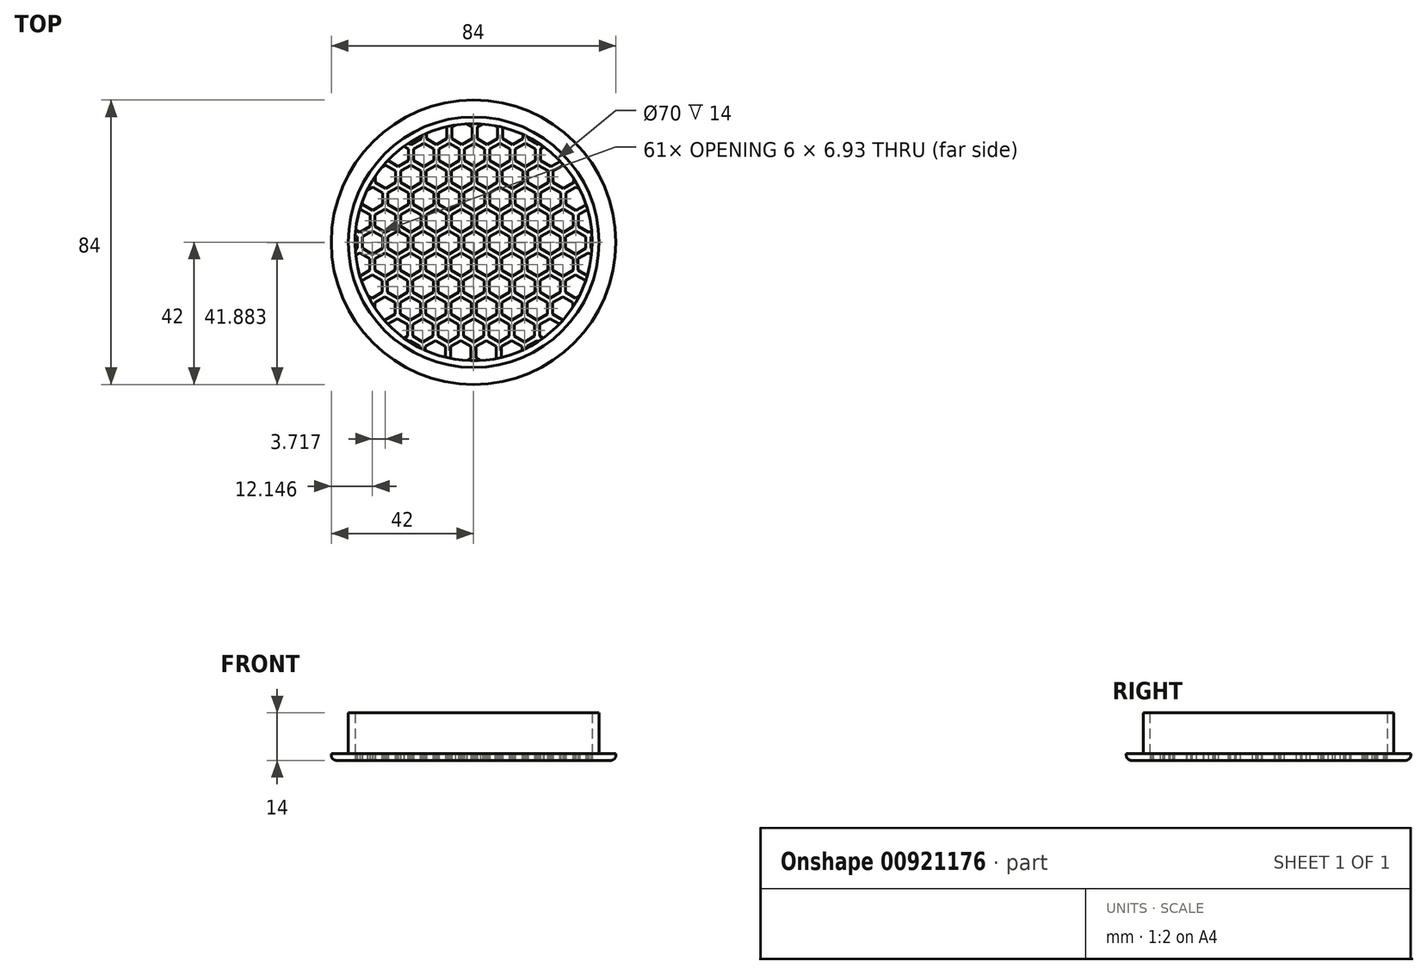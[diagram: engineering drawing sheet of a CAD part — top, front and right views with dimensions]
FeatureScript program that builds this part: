
annotation { "Feature Type Name" : "Feature", "Feature Type Description" : "" }
export const myFeature = defineFeature(function(context is Context, id is Id, definition is map)
    precondition{}
    {
        {
            var Q0;
            Q0=qCreatedBy(makeId("Top.planeOp"),FACE);
            var sketch = newSketch(context, id + "F0", { "sketchPlane" : qUnion([Q0])});
            skCircle(sketch, "E0", {"center": v(0, 0) * mm, "radius": 42 * mm});
            skCircle(sketch, "E1", {"center": v(0, 0) * mm, "radius": 35 * mm});
            skSolve(sketch);
        }
        {
            var Q0;
            Q0=makeQuery(id+"F0.imprint","IMPRINT",FACE,{"disambiguationData":[TD([[makeQuery(id+"F0.imprint","IMPRINT",EDGE,{"derivedFrom":sQuery(id+"F0.wireOp",EDGE,"E0")}),1.0]])]});
            extrude(context, id + "F1", {"entities" : qUnion([Q0]), "depth" : 2 * mm, "offsetDistance" : 25 * mm});
        }
        {
            var Q0;
            Q0=makeQuery(id+"F1.opExtrude","CAP_EDGE",EDGE,{"disambiguationData":[OSD([sQuery(id+"F0.wireOp",EDGE,"E0")])],"isStart":true});
            fillet(context, id + "F2", {"entities" : qUnion([Q0]), "radius" : 1.5 * mm, "tangentPropagation" : true, "allowEdgeOverflow" : false});
        }
        {
            var Q0;
            Q0=makeQuery(id+"F1.opExtrude","CAP_FACE",FACE,{"disambiguationData":[OSD([sQuery(id+"F0.wireOp",EDGE,"E0"),sQuery(id+"F0.wireOp",EDGE,"E1")])],"isStart":false});
            var sketch = newSketch(context, id + "F3", { "sketchPlane" : qUnion([Q0])});
            skCircle(sketch, "E2", {"center": v(0, 0) * mm, "radius": 37 * mm});
            skCircle(sketch, "E3", {"center": v(0, 0) * mm, "radius": 35 * mm});
            skSolve(sketch);
        }
        {
            var Q0;
            Q0=makeQuery(id+"F3.imprint","IMPRINT",FACE,{"disambiguationData":[TD([[makeQuery(id+"F3.imprint","IMPRINT",EDGE,{"derivedFrom":sQuery(id+"F3.wireOp",EDGE,"E2")}),1.0]])]});
            extrude(context, id + "F4", {"entities" : qUnion([Q0]), "operationType" : NewBodyOperationType.ADD, "depth" : 12 * mm, "offsetDistance" : 25 * mm});
        }
        {
            var Q0;
            Q0=qCreatedBy(makeId("Top.planeOp"),FACE);
            var sketch = newSketch(context, id + "F5", { "sketchPlane" : qUnion([Q0])});
            skLineSegment(sketch, "E4.4.0.0", {"start": v(-56.27, -29.03) * mm, "end": v(-53.27, -30.77) * mm});
            skPoint(sketch, "E4.4.0.1", {"position": v(-54.77, -35.1) * mm});
            skCircle(sketch, "E4.4.0.2", {"center": v(-56.27, -32.5) * mm, "radius": 3 * mm, "construction": true});
            skLineSegment(sketch, "E4.4.0.3", {"start": v(-53.27, -30.77) * mm, "end": v(-53.27, -34.23) * mm});
            skLineSegment(sketch, "E4.4.0.4", {"start": v(-59.27, -34.23) * mm, "end": v(-59.27, -30.77) * mm});
            skLineSegment(sketch, "E4.4.0.5", {"start": v(-59.27, -30.77) * mm, "end": v(-56.27, -29.03) * mm});
            skLineSegment(sketch, "E4.4.0.6", {"start": v(-53.27, -34.23) * mm, "end": v(-56.27, -35.96) * mm});
            skLineSegment(sketch, "E4.4.0.7", {"start": v(-56.27, -35.96) * mm, "end": v(-59.27, -34.23) * mm});
            skLineSegment(sketch, "E5.0.1.0", {"start": v(-55.49, -27.75) * mm, "end": v(-55.49, -24.29) * mm});
            skCircle(sketch, "E5.0.1.1", {"center": v(-52.49, -26.02) * mm, "radius": 3 * mm, "construction": true});
            skPoint(sketch, "E5.0.1.2", {"position": v(-50.99, -28.62) * mm});
            skLineSegment(sketch, "E5.0.1.3", {"start": v(-52.49, -29.49) * mm, "end": v(-55.49, -27.75) * mm});
            skLineSegment(sketch, "E5.0.1.4", {"start": v(-52.49, -22.56) * mm, "end": v(-49.49, -24.29) * mm});
            skLineSegment(sketch, "E5.0.1.5", {"start": v(-55.49, -24.29) * mm, "end": v(-52.49, -22.56) * mm});
            skLineSegment(sketch, "E5.0.1.6", {"start": v(-49.49, -24.29) * mm, "end": v(-49.49, -27.75) * mm});
            skLineSegment(sketch, "E5.0.1.7", {"start": v(-49.49, -27.75) * mm, "end": v(-52.49, -29.49) * mm});
            skLineSegment(sketch, "E5.0.2.0", {"start": v(-51.7, -21.28) * mm, "end": v(-51.7, -17.81) * mm});
            skCircle(sketch, "E5.0.2.1", {"center": v(-48.7, -19.55) * mm, "radius": 3 * mm, "construction": true});
            skPoint(sketch, "E5.0.2.2", {"position": v(-47.2, -22.14) * mm});
            skLineSegment(sketch, "E5.0.2.3", {"start": v(-48.7, -23) * mm, "end": v(-51.7, -21.28) * mm});
            skLineSegment(sketch, "E5.0.2.4", {"start": v(-48.7, -16.08) * mm, "end": v(-45.7, -17.81) * mm});
            skLineSegment(sketch, "E5.0.2.5", {"start": v(-51.7, -17.81) * mm, "end": v(-48.7, -16.08) * mm});
            skLineSegment(sketch, "E5.0.2.6", {"start": v(-45.7, -17.81) * mm, "end": v(-45.7, -21.28) * mm});
            skLineSegment(sketch, "E5.0.2.7", {"start": v(-45.7, -21.28) * mm, "end": v(-48.7, -23) * mm});
            skLineSegment(sketch, "E5.0.3.0", {"start": v(-47.92, -14.8) * mm, "end": v(-47.92, -11.34) * mm});
            skCircle(sketch, "E5.0.3.1", {"center": v(-44.92, -13.07) * mm, "radius": 3 * mm, "construction": true});
            skPoint(sketch, "E5.0.3.2", {"position": v(-43.42, -15.67) * mm});
            skLineSegment(sketch, "E5.0.3.3", {"start": v(-44.92, -16.53) * mm, "end": v(-47.92, -14.8) * mm});
            skLineSegment(sketch, "E5.0.3.4", {"start": v(-44.92, -9.6) * mm, "end": v(-41.92, -11.34) * mm});
            skLineSegment(sketch, "E5.0.3.5", {"start": v(-47.92, -11.34) * mm, "end": v(-44.92, -9.6) * mm});
            skLineSegment(sketch, "E5.0.3.6", {"start": v(-41.92, -11.34) * mm, "end": v(-41.92, -14.8) * mm});
            skLineSegment(sketch, "E5.0.3.7", {"start": v(-41.92, -14.8) * mm, "end": v(-44.92, -16.53) * mm});
            skLineSegment(sketch, "E5.0.4.0", {"start": v(-44.14, -8.33) * mm, "end": v(-44.14, -4.86) * mm});
            skCircle(sketch, "E5.0.4.1", {"center": v(-41.14, -6.6) * mm, "radius": 3 * mm, "construction": true});
            skPoint(sketch, "E5.0.4.2", {"position": v(-39.64, -9.2) * mm});
            skLineSegment(sketch, "E5.0.4.3", {"start": v(-41.14, -10.06) * mm, "end": v(-44.14, -8.33) * mm});
            skLineSegment(sketch, "E5.0.4.4", {"start": v(-41.14, -3.13) * mm, "end": v(-38.14, -4.86) * mm});
            skLineSegment(sketch, "E5.0.4.5", {"start": v(-44.14, -4.86) * mm, "end": v(-41.14, -3.13) * mm});
            skLineSegment(sketch, "E5.0.4.6", {"start": v(-38.14, -4.86) * mm, "end": v(-38.14, -8.33) * mm});
            skLineSegment(sketch, "E5.0.4.7", {"start": v(-38.14, -8.33) * mm, "end": v(-41.14, -10.06) * mm});
            skLineSegment(sketch, "E5.0.5.0", {"start": v(-40.35, -1.85) * mm, "end": v(-40.35, 1.62) * mm});
            skCircle(sketch, "E5.0.5.1", {"center": v(-37.35, -0.12) * mm, "radius": 3 * mm, "construction": true});
            skPoint(sketch, "E5.0.5.2", {"position": v(-35.85, -2.72) * mm});
            skLineSegment(sketch, "E5.0.5.3", {"start": v(-37.35, -3.58) * mm, "end": v(-40.35, -1.85) * mm});
            skLineSegment(sketch, "E5.0.5.4", {"start": v(-37.35, 3.35) * mm, "end": v(-34.35, 1.62) * mm});
            skLineSegment(sketch, "E5.0.5.5", {"start": v(-40.35, 1.62) * mm, "end": v(-37.35, 3.35) * mm});
            skLineSegment(sketch, "E5.0.5.6", {"start": v(-34.35, 1.62) * mm, "end": v(-34.35, -1.85) * mm});
            skLineSegment(sketch, "E5.0.5.7", {"start": v(-34.35, -1.85) * mm, "end": v(-37.35, -3.58) * mm});
            skLineSegment(sketch, "E5.0.6.0", {"start": v(-36.57, 4.63) * mm, "end": v(-36.57, 8.1) * mm});
            skCircle(sketch, "E5.0.6.1", {"center": v(-33.57, 6.36) * mm, "radius": 3 * mm, "construction": true});
            skPoint(sketch, "E5.0.6.2", {"position": v(-32.07, 3.76) * mm});
            skLineSegment(sketch, "E5.0.6.3", {"start": v(-33.57, 2.9) * mm, "end": v(-36.57, 4.63) * mm});
            skLineSegment(sketch, "E5.0.6.4", {"start": v(-33.57, 9.82) * mm, "end": v(-30.57, 8.1) * mm});
            skLineSegment(sketch, "E5.0.6.5", {"start": v(-36.57, 8.1) * mm, "end": v(-33.57, 9.82) * mm});
            skLineSegment(sketch, "E5.0.6.6", {"start": v(-30.57, 8.1) * mm, "end": v(-30.57, 4.63) * mm});
            skLineSegment(sketch, "E5.0.6.7", {"start": v(-30.57, 4.63) * mm, "end": v(-33.57, 2.9) * mm});
            skLineSegment(sketch, "E5.0.7.0", {"start": v(-32.79, 11.1) * mm, "end": v(-32.79, 14.57) * mm});
            skCircle(sketch, "E5.0.7.1", {"center": v(-29.79, 12.84) * mm, "radius": 3 * mm, "construction": true});
            skPoint(sketch, "E5.0.7.2", {"position": v(-28.29, 10.24) * mm});
            skLineSegment(sketch, "E5.0.7.3", {"start": v(-29.79, 9.37) * mm, "end": v(-32.79, 11.1) * mm});
            skLineSegment(sketch, "E5.0.7.4", {"start": v(-29.79, 16.3) * mm, "end": v(-26.79, 14.57) * mm});
            skLineSegment(sketch, "E5.0.7.5", {"start": v(-32.79, 14.57) * mm, "end": v(-29.79, 16.3) * mm});
            skLineSegment(sketch, "E5.0.7.6", {"start": v(-26.79, 14.57) * mm, "end": v(-26.79, 11.1) * mm});
            skLineSegment(sketch, "E5.0.7.7", {"start": v(-26.79, 11.1) * mm, "end": v(-29.79, 9.37) * mm});
            skLineSegment(sketch, "E5.0.8.0", {"start": v(-29, 17.58) * mm, "end": v(-29, 21.04) * mm});
            skCircle(sketch, "E5.0.8.1", {"center": v(-26, 19.31) * mm, "radius": 3 * mm, "construction": true});
            skPoint(sketch, "E5.0.8.2", {"position": v(-24.5, 16.71) * mm});
            skLineSegment(sketch, "E5.0.8.3", {"start": v(-26, 15.85) * mm, "end": v(-29, 17.58) * mm});
            skLineSegment(sketch, "E5.0.8.4", {"start": v(-26, 22.78) * mm, "end": v(-23, 21.04) * mm});
            skLineSegment(sketch, "E5.0.8.5", {"start": v(-29, 21.04) * mm, "end": v(-26, 22.78) * mm});
            skLineSegment(sketch, "E5.0.8.6", {"start": v(-23, 21.04) * mm, "end": v(-23, 17.58) * mm});
            skLineSegment(sketch, "E5.0.8.7", {"start": v(-23, 17.58) * mm, "end": v(-26, 15.85) * mm});
            skLineSegment(sketch, "E5.0.9.0", {"start": v(-25.22, 24.06) * mm, "end": v(-25.22, 27.52) * mm});
            skCircle(sketch, "E5.0.9.1", {"center": v(-22.22, 25.79) * mm, "radius": 3 * mm, "construction": true});
            skPoint(sketch, "E5.0.9.2", {"position": v(-20.72, 23.19) * mm});
            skLineSegment(sketch, "E5.0.9.3", {"start": v(-22.22, 22.32) * mm, "end": v(-25.22, 24.06) * mm});
            skLineSegment(sketch, "E5.0.9.4", {"start": v(-22.22, 29.25) * mm, "end": v(-19.22, 27.52) * mm});
            skLineSegment(sketch, "E5.0.9.5", {"start": v(-25.22, 27.52) * mm, "end": v(-22.22, 29.25) * mm});
            skLineSegment(sketch, "E5.0.9.6", {"start": v(-19.22, 27.52) * mm, "end": v(-19.22, 24.06) * mm});
            skLineSegment(sketch, "E5.0.9.7", {"start": v(-19.22, 24.06) * mm, "end": v(-22.22, 22.32) * mm});
            skLineSegment(sketch, "E5.1.0.0", {"start": v(-51.77, -34.23) * mm, "end": v(-51.77, -30.77) * mm});
            skCircle(sketch, "E5.1.0.1", {"center": v(-48.77, -32.5) * mm, "radius": 3 * mm, "construction": true});
            skPoint(sketch, "E5.1.0.2", {"position": v(-47.27, -35.1) * mm});
            skLineSegment(sketch, "E5.1.0.3", {"start": v(-48.77, -35.96) * mm, "end": v(-51.77, -34.23) * mm});
            skLineSegment(sketch, "E5.1.0.4", {"start": v(-48.77, -29.03) * mm, "end": v(-45.77, -30.77) * mm});
            skLineSegment(sketch, "E5.1.0.5", {"start": v(-51.77, -30.77) * mm, "end": v(-48.77, -29.03) * mm});
            skLineSegment(sketch, "E5.1.0.6", {"start": v(-45.77, -30.77) * mm, "end": v(-45.77, -34.23) * mm});
            skLineSegment(sketch, "E5.1.0.7", {"start": v(-45.77, -34.23) * mm, "end": v(-48.77, -35.96) * mm});
            skLineSegment(sketch, "E5.1.1.0", {"start": v(-47.99, -27.75) * mm, "end": v(-47.99, -24.29) * mm});
            skCircle(sketch, "E5.1.1.1", {"center": v(-44.99, -26.02) * mm, "radius": 3 * mm, "construction": true});
            skPoint(sketch, "E5.1.1.2", {"position": v(-43.49, -28.62) * mm});
            skLineSegment(sketch, "E5.1.1.3", {"start": v(-44.99, -29.49) * mm, "end": v(-47.99, -27.75) * mm});
            skLineSegment(sketch, "E5.1.1.4", {"start": v(-44.99, -22.56) * mm, "end": v(-41.99, -24.29) * mm});
            skLineSegment(sketch, "E5.1.1.5", {"start": v(-47.99, -24.29) * mm, "end": v(-44.99, -22.56) * mm});
            skLineSegment(sketch, "E5.1.1.6", {"start": v(-41.99, -24.29) * mm, "end": v(-41.99, -27.75) * mm});
            skLineSegment(sketch, "E5.1.1.7", {"start": v(-41.99, -27.75) * mm, "end": v(-44.99, -29.49) * mm});
            skLineSegment(sketch, "E5.1.2.0", {"start": v(-44.2, -21.28) * mm, "end": v(-44.2, -17.81) * mm});
            skCircle(sketch, "E5.1.2.1", {"center": v(-41.2, -19.55) * mm, "radius": 3 * mm, "construction": true});
            skPoint(sketch, "E5.1.2.2", {"position": v(-39.7, -22.14) * mm});
            skLineSegment(sketch, "E5.1.2.3", {"start": v(-41.2, -23) * mm, "end": v(-44.2, -21.28) * mm});
            skLineSegment(sketch, "E5.1.2.4", {"start": v(-41.2, -16.08) * mm, "end": v(-38.2, -17.81) * mm});
            skLineSegment(sketch, "E5.1.2.5", {"start": v(-44.2, -17.81) * mm, "end": v(-41.2, -16.08) * mm});
            skLineSegment(sketch, "E5.1.2.6", {"start": v(-38.2, -17.81) * mm, "end": v(-38.2, -21.28) * mm});
            skLineSegment(sketch, "E5.1.2.7", {"start": v(-38.2, -21.28) * mm, "end": v(-41.2, -23) * mm});
            skLineSegment(sketch, "E5.1.3.0", {"start": v(-40.42, -14.8) * mm, "end": v(-40.42, -11.34) * mm});
            skCircle(sketch, "E5.1.3.1", {"center": v(-37.42, -13.07) * mm, "radius": 3 * mm, "construction": true});
            skPoint(sketch, "E5.1.3.2", {"position": v(-35.92, -15.67) * mm});
            skLineSegment(sketch, "E5.1.3.3", {"start": v(-37.42, -16.53) * mm, "end": v(-40.42, -14.8) * mm});
            skLineSegment(sketch, "E5.1.3.4", {"start": v(-37.42, -9.6) * mm, "end": v(-34.42, -11.34) * mm});
            skLineSegment(sketch, "E5.1.3.5", {"start": v(-40.42, -11.34) * mm, "end": v(-37.42, -9.6) * mm});
            skLineSegment(sketch, "E5.1.3.6", {"start": v(-34.42, -11.34) * mm, "end": v(-34.42, -14.8) * mm});
            skLineSegment(sketch, "E5.1.3.7", {"start": v(-34.42, -14.8) * mm, "end": v(-37.42, -16.53) * mm});
            skLineSegment(sketch, "E5.1.4.0", {"start": v(-36.64, -8.33) * mm, "end": v(-36.64, -4.86) * mm});
            skCircle(sketch, "E5.1.4.1", {"center": v(-33.64, -6.6) * mm, "radius": 3 * mm, "construction": true});
            skPoint(sketch, "E5.1.4.2", {"position": v(-32.14, -9.2) * mm});
            skLineSegment(sketch, "E5.1.4.3", {"start": v(-33.64, -10.06) * mm, "end": v(-36.64, -8.33) * mm});
            skLineSegment(sketch, "E5.1.4.4", {"start": v(-33.64, -3.13) * mm, "end": v(-30.64, -4.86) * mm});
            skLineSegment(sketch, "E5.1.4.5", {"start": v(-36.64, -4.86) * mm, "end": v(-33.64, -3.13) * mm});
            skLineSegment(sketch, "E5.1.4.6", {"start": v(-30.64, -4.86) * mm, "end": v(-30.64, -8.33) * mm});
            skLineSegment(sketch, "E5.1.4.7", {"start": v(-30.64, -8.33) * mm, "end": v(-33.64, -10.06) * mm});
            skLineSegment(sketch, "E5.1.5.0", {"start": v(-32.85, -1.85) * mm, "end": v(-32.85, 1.62) * mm});
            skCircle(sketch, "E5.1.5.1", {"center": v(-29.85, -0.12) * mm, "radius": 3 * mm, "construction": true});
            skPoint(sketch, "E5.1.5.2", {"position": v(-28.35, -2.72) * mm});
            skLineSegment(sketch, "E5.1.5.3", {"start": v(-29.85, -3.58) * mm, "end": v(-32.85, -1.85) * mm});
            skLineSegment(sketch, "E5.1.5.4", {"start": v(-29.85, 3.35) * mm, "end": v(-26.85, 1.62) * mm});
            skLineSegment(sketch, "E5.1.5.5", {"start": v(-32.85, 1.62) * mm, "end": v(-29.85, 3.35) * mm});
            skLineSegment(sketch, "E5.1.5.6", {"start": v(-26.85, 1.62) * mm, "end": v(-26.85, -1.85) * mm});
            skLineSegment(sketch, "E5.1.5.7", {"start": v(-26.85, -1.85) * mm, "end": v(-29.85, -3.58) * mm});
            skLineSegment(sketch, "E5.1.6.0", {"start": v(-29.07, 4.63) * mm, "end": v(-29.07, 8.1) * mm});
            skCircle(sketch, "E5.1.6.1", {"center": v(-26.07, 6.36) * mm, "radius": 3 * mm, "construction": true});
            skPoint(sketch, "E5.1.6.2", {"position": v(-24.57, 3.76) * mm});
            skLineSegment(sketch, "E5.1.6.3", {"start": v(-26.07, 2.9) * mm, "end": v(-29.07, 4.63) * mm});
            skLineSegment(sketch, "E5.1.6.4", {"start": v(-26.07, 9.82) * mm, "end": v(-23.07, 8.1) * mm});
            skLineSegment(sketch, "E5.1.6.5", {"start": v(-29.07, 8.1) * mm, "end": v(-26.07, 9.82) * mm});
            skLineSegment(sketch, "E5.1.6.6", {"start": v(-23.07, 8.1) * mm, "end": v(-23.07, 4.63) * mm});
            skLineSegment(sketch, "E5.1.6.7", {"start": v(-23.07, 4.63) * mm, "end": v(-26.07, 2.9) * mm});
            skLineSegment(sketch, "E5.1.7.0", {"start": v(-25.29, 11.1) * mm, "end": v(-25.29, 14.57) * mm});
            skCircle(sketch, "E5.1.7.1", {"center": v(-22.29, 12.84) * mm, "radius": 3 * mm, "construction": true});
            skPoint(sketch, "E5.1.7.2", {"position": v(-20.79, 10.24) * mm});
            skLineSegment(sketch, "E5.1.7.3", {"start": v(-22.29, 9.37) * mm, "end": v(-25.29, 11.1) * mm});
            skLineSegment(sketch, "E5.1.7.4", {"start": v(-22.29, 16.3) * mm, "end": v(-19.29, 14.57) * mm});
            skLineSegment(sketch, "E5.1.7.5", {"start": v(-25.29, 14.57) * mm, "end": v(-22.29, 16.3) * mm});
            skLineSegment(sketch, "E5.1.7.6", {"start": v(-19.29, 14.57) * mm, "end": v(-19.29, 11.1) * mm});
            skLineSegment(sketch, "E5.1.7.7", {"start": v(-19.29, 11.1) * mm, "end": v(-22.29, 9.37) * mm});
            skLineSegment(sketch, "E5.1.8.0", {"start": v(-21.5, 17.58) * mm, "end": v(-21.5, 21.04) * mm});
            skCircle(sketch, "E5.1.8.1", {"center": v(-18.5, 19.31) * mm, "radius": 3 * mm, "construction": true});
            skPoint(sketch, "E5.1.8.2", {"position": v(-17, 16.71) * mm});
            skLineSegment(sketch, "E5.1.8.3", {"start": v(-18.5, 15.85) * mm, "end": v(-21.5, 17.58) * mm});
            skLineSegment(sketch, "E5.1.8.4", {"start": v(-18.5, 22.78) * mm, "end": v(-15.5, 21.04) * mm});
            skLineSegment(sketch, "E5.1.8.5", {"start": v(-21.5, 21.04) * mm, "end": v(-18.5, 22.78) * mm});
            skLineSegment(sketch, "E5.1.8.6", {"start": v(-15.5, 21.04) * mm, "end": v(-15.5, 17.58) * mm});
            skLineSegment(sketch, "E5.1.8.7", {"start": v(-15.5, 17.58) * mm, "end": v(-18.5, 15.85) * mm});
            skLineSegment(sketch, "E5.1.9.0", {"start": v(-17.72, 24.06) * mm, "end": v(-17.72, 27.52) * mm});
            skCircle(sketch, "E5.1.9.1", {"center": v(-14.72, 25.79) * mm, "radius": 3 * mm, "construction": true});
            skPoint(sketch, "E5.1.9.2", {"position": v(-13.22, 23.19) * mm});
            skLineSegment(sketch, "E5.1.9.3", {"start": v(-14.72, 22.32) * mm, "end": v(-17.72, 24.06) * mm});
            skLineSegment(sketch, "E5.1.9.4", {"start": v(-14.72, 29.25) * mm, "end": v(-11.72, 27.52) * mm});
            skLineSegment(sketch, "E5.1.9.5", {"start": v(-17.72, 27.52) * mm, "end": v(-14.72, 29.25) * mm});
            skLineSegment(sketch, "E5.1.9.6", {"start": v(-11.72, 27.52) * mm, "end": v(-11.72, 24.06) * mm});
            skLineSegment(sketch, "E5.1.9.7", {"start": v(-11.72, 24.06) * mm, "end": v(-14.72, 22.32) * mm});
            skLineSegment(sketch, "E5.2.0.0", {"start": v(-44.27, -34.23) * mm, "end": v(-44.27, -30.77) * mm});
            skCircle(sketch, "E5.2.0.1", {"center": v(-41.27, -32.5) * mm, "radius": 3 * mm, "construction": true});
            skPoint(sketch, "E5.2.0.2", {"position": v(-39.77, -35.1) * mm});
            skLineSegment(sketch, "E5.2.0.3", {"start": v(-41.27, -35.96) * mm, "end": v(-44.27, -34.23) * mm});
            skLineSegment(sketch, "E5.2.0.4", {"start": v(-41.27, -29.03) * mm, "end": v(-38.27, -30.77) * mm});
            skLineSegment(sketch, "E5.2.0.5", {"start": v(-44.27, -30.77) * mm, "end": v(-41.27, -29.03) * mm});
            skLineSegment(sketch, "E5.2.0.6", {"start": v(-38.27, -30.77) * mm, "end": v(-38.27, -34.23) * mm});
            skLineSegment(sketch, "E5.2.0.7", {"start": v(-38.27, -34.23) * mm, "end": v(-41.27, -35.96) * mm});
            skLineSegment(sketch, "E5.2.1.0", {"start": v(-40.49, -27.75) * mm, "end": v(-40.49, -24.29) * mm});
            skCircle(sketch, "E5.2.1.1", {"center": v(-37.49, -26.02) * mm, "radius": 3 * mm, "construction": true});
            skPoint(sketch, "E5.2.1.2", {"position": v(-35.99, -28.62) * mm});
            skLineSegment(sketch, "E5.2.1.3", {"start": v(-37.49, -29.49) * mm, "end": v(-40.49, -27.75) * mm});
            skLineSegment(sketch, "E5.2.1.4", {"start": v(-37.49, -22.56) * mm, "end": v(-34.49, -24.29) * mm});
            skLineSegment(sketch, "E5.2.1.5", {"start": v(-40.49, -24.29) * mm, "end": v(-37.49, -22.56) * mm});
            skLineSegment(sketch, "E5.2.1.6", {"start": v(-34.49, -24.29) * mm, "end": v(-34.49, -27.75) * mm});
            skLineSegment(sketch, "E5.2.1.7", {"start": v(-34.49, -27.75) * mm, "end": v(-37.49, -29.49) * mm});
            skLineSegment(sketch, "E5.2.2.0", {"start": v(-36.7, -21.28) * mm, "end": v(-36.7, -17.81) * mm});
            skCircle(sketch, "E5.2.2.1", {"center": v(-33.7, -19.55) * mm, "radius": 3 * mm, "construction": true});
            skPoint(sketch, "E5.2.2.2", {"position": v(-32.2, -22.14) * mm});
            skLineSegment(sketch, "E5.2.2.3", {"start": v(-33.7, -23) * mm, "end": v(-36.7, -21.28) * mm});
            skLineSegment(sketch, "E5.2.2.4", {"start": v(-33.7, -16.08) * mm, "end": v(-30.7, -17.81) * mm});
            skLineSegment(sketch, "E5.2.2.5", {"start": v(-36.7, -17.81) * mm, "end": v(-33.7, -16.08) * mm});
            skLineSegment(sketch, "E5.2.2.6", {"start": v(-30.7, -17.81) * mm, "end": v(-30.7, -21.28) * mm});
            skLineSegment(sketch, "E5.2.2.7", {"start": v(-30.7, -21.28) * mm, "end": v(-33.7, -23) * mm});
            skLineSegment(sketch, "E5.2.3.0", {"start": v(-32.92, -14.8) * mm, "end": v(-32.92, -11.34) * mm});
            skCircle(sketch, "E5.2.3.1", {"center": v(-29.92, -13.07) * mm, "radius": 3 * mm, "construction": true});
            skPoint(sketch, "E5.2.3.2", {"position": v(-28.42, -15.67) * mm});
            skLineSegment(sketch, "E5.2.3.3", {"start": v(-29.92, -16.53) * mm, "end": v(-32.92, -14.8) * mm});
            skLineSegment(sketch, "E5.2.3.4", {"start": v(-29.92, -9.6) * mm, "end": v(-26.92, -11.34) * mm});
            skLineSegment(sketch, "E5.2.3.5", {"start": v(-32.92, -11.34) * mm, "end": v(-29.92, -9.6) * mm});
            skLineSegment(sketch, "E5.2.3.6", {"start": v(-26.92, -11.34) * mm, "end": v(-26.92, -14.8) * mm});
            skLineSegment(sketch, "E5.2.3.7", {"start": v(-26.92, -14.8) * mm, "end": v(-29.92, -16.53) * mm});
            skLineSegment(sketch, "E5.2.4.0", {"start": v(-29.14, -8.33) * mm, "end": v(-29.14, -4.86) * mm});
            skCircle(sketch, "E5.2.4.1", {"center": v(-26.14, -6.6) * mm, "radius": 3 * mm, "construction": true});
            skPoint(sketch, "E5.2.4.2", {"position": v(-24.64, -9.2) * mm});
            skLineSegment(sketch, "E5.2.4.3", {"start": v(-26.14, -10.06) * mm, "end": v(-29.14, -8.33) * mm});
            skLineSegment(sketch, "E5.2.4.4", {"start": v(-26.14, -3.13) * mm, "end": v(-23.14, -4.86) * mm});
            skLineSegment(sketch, "E5.2.4.5", {"start": v(-29.14, -4.86) * mm, "end": v(-26.14, -3.13) * mm});
            skLineSegment(sketch, "E5.2.4.6", {"start": v(-23.14, -4.86) * mm, "end": v(-23.14, -8.33) * mm});
            skLineSegment(sketch, "E5.2.4.7", {"start": v(-23.14, -8.33) * mm, "end": v(-26.14, -10.06) * mm});
            skLineSegment(sketch, "E5.2.5.0", {"start": v(-25.35, -1.85) * mm, "end": v(-25.35, 1.62) * mm});
            skCircle(sketch, "E5.2.5.1", {"center": v(-22.35, -0.12) * mm, "radius": 3 * mm, "construction": true});
            skPoint(sketch, "E5.2.5.2", {"position": v(-20.85, -2.72) * mm});
            skLineSegment(sketch, "E5.2.5.3", {"start": v(-22.35, -3.58) * mm, "end": v(-25.35, -1.85) * mm});
            skLineSegment(sketch, "E5.2.5.4", {"start": v(-22.35, 3.35) * mm, "end": v(-19.35, 1.62) * mm});
            skLineSegment(sketch, "E5.2.5.5", {"start": v(-25.35, 1.62) * mm, "end": v(-22.35, 3.35) * mm});
            skLineSegment(sketch, "E5.2.5.6", {"start": v(-19.35, 1.62) * mm, "end": v(-19.35, -1.85) * mm});
            skLineSegment(sketch, "E5.2.5.7", {"start": v(-19.35, -1.85) * mm, "end": v(-22.35, -3.58) * mm});
            skLineSegment(sketch, "E5.2.6.0", {"start": v(-21.57, 4.63) * mm, "end": v(-21.57, 8.1) * mm});
            skCircle(sketch, "E5.2.6.1", {"center": v(-18.57, 6.36) * mm, "radius": 3 * mm, "construction": true});
            skPoint(sketch, "E5.2.6.2", {"position": v(-17.07, 3.76) * mm});
            skLineSegment(sketch, "E5.2.6.3", {"start": v(-18.57, 2.9) * mm, "end": v(-21.57, 4.63) * mm});
            skLineSegment(sketch, "E5.2.6.4", {"start": v(-18.57, 9.82) * mm, "end": v(-15.57, 8.1) * mm});
            skLineSegment(sketch, "E5.2.6.5", {"start": v(-21.57, 8.1) * mm, "end": v(-18.57, 9.82) * mm});
            skLineSegment(sketch, "E5.2.6.6", {"start": v(-15.57, 8.1) * mm, "end": v(-15.57, 4.63) * mm});
            skLineSegment(sketch, "E5.2.6.7", {"start": v(-15.57, 4.63) * mm, "end": v(-18.57, 2.9) * mm});
            skLineSegment(sketch, "E5.2.7.0", {"start": v(-17.79, 11.1) * mm, "end": v(-17.79, 14.57) * mm});
            skCircle(sketch, "E5.2.7.1", {"center": v(-14.79, 12.84) * mm, "radius": 3 * mm, "construction": true});
            skPoint(sketch, "E5.2.7.2", {"position": v(-13.29, 10.24) * mm});
            skLineSegment(sketch, "E5.2.7.3", {"start": v(-14.79, 9.37) * mm, "end": v(-17.79, 11.1) * mm});
            skLineSegment(sketch, "E5.2.7.4", {"start": v(-14.79, 16.3) * mm, "end": v(-11.79, 14.57) * mm});
            skLineSegment(sketch, "E5.2.7.5", {"start": v(-17.79, 14.57) * mm, "end": v(-14.79, 16.3) * mm});
            skLineSegment(sketch, "E5.2.7.6", {"start": v(-11.79, 14.57) * mm, "end": v(-11.79, 11.1) * mm});
            skLineSegment(sketch, "E5.2.7.7", {"start": v(-11.79, 11.1) * mm, "end": v(-14.79, 9.37) * mm});
            skLineSegment(sketch, "E5.2.8.0", {"start": v(-14, 17.58) * mm, "end": v(-14, 21.04) * mm});
            skCircle(sketch, "E5.2.8.1", {"center": v(-11, 19.31) * mm, "radius": 3 * mm, "construction": true});
            skPoint(sketch, "E5.2.8.2", {"position": v(-9.5, 16.71) * mm});
            skLineSegment(sketch, "E5.2.8.3", {"start": v(-11, 15.85) * mm, "end": v(-14, 17.58) * mm});
            skLineSegment(sketch, "E5.2.8.4", {"start": v(-11, 22.78) * mm, "end": v(-8, 21.04) * mm});
            skLineSegment(sketch, "E5.2.8.5", {"start": v(-14, 21.04) * mm, "end": v(-11, 22.78) * mm});
            skLineSegment(sketch, "E5.2.8.6", {"start": v(-8, 21.04) * mm, "end": v(-8, 17.58) * mm});
            skLineSegment(sketch, "E5.2.8.7", {"start": v(-8, 17.58) * mm, "end": v(-11, 15.85) * mm});
            skLineSegment(sketch, "E5.2.9.0", {"start": v(-10.22, 24.06) * mm, "end": v(-10.22, 27.52) * mm});
            skCircle(sketch, "E5.2.9.1", {"center": v(-7.22, 25.79) * mm, "radius": 3 * mm, "construction": true});
            skPoint(sketch, "E5.2.9.2", {"position": v(-5.72, 23.19) * mm});
            skLineSegment(sketch, "E5.2.9.3", {"start": v(-7.22, 22.32) * mm, "end": v(-10.22, 24.06) * mm});
            skLineSegment(sketch, "E5.2.9.4", {"start": v(-7.22, 29.25) * mm, "end": v(-4.22, 27.52) * mm});
            skLineSegment(sketch, "E5.2.9.5", {"start": v(-10.22, 27.52) * mm, "end": v(-7.22, 29.25) * mm});
            skLineSegment(sketch, "E5.2.9.6", {"start": v(-4.22, 27.52) * mm, "end": v(-4.22, 24.06) * mm});
            skLineSegment(sketch, "E5.2.9.7", {"start": v(-4.22, 24.06) * mm, "end": v(-7.22, 22.32) * mm});
            skLineSegment(sketch, "E5.3.0.0", {"start": v(-36.77, -34.23) * mm, "end": v(-36.77, -30.77) * mm});
            skCircle(sketch, "E5.3.0.1", {"center": v(-33.77, -32.5) * mm, "radius": 3 * mm, "construction": true});
            skPoint(sketch, "E5.3.0.2", {"position": v(-32.27, -35.1) * mm});
            skLineSegment(sketch, "E5.3.0.3", {"start": v(-33.77, -35.96) * mm, "end": v(-36.77, -34.23) * mm});
            skLineSegment(sketch, "E5.3.0.4", {"start": v(-33.77, -29.03) * mm, "end": v(-30.77, -30.77) * mm});
            skLineSegment(sketch, "E5.3.0.5", {"start": v(-36.77, -30.77) * mm, "end": v(-33.77, -29.03) * mm});
            skLineSegment(sketch, "E5.3.0.6", {"start": v(-30.77, -30.77) * mm, "end": v(-30.77, -34.23) * mm});
            skLineSegment(sketch, "E5.3.0.7", {"start": v(-30.77, -34.23) * mm, "end": v(-33.77, -35.96) * mm});
            skLineSegment(sketch, "E5.3.1.0", {"start": v(-32.99, -27.75) * mm, "end": v(-32.99, -24.29) * mm});
            skCircle(sketch, "E5.3.1.1", {"center": v(-29.99, -26.02) * mm, "radius": 3 * mm, "construction": true});
            skPoint(sketch, "E5.3.1.2", {"position": v(-28.49, -28.62) * mm});
            skLineSegment(sketch, "E5.3.1.3", {"start": v(-29.99, -29.49) * mm, "end": v(-32.99, -27.75) * mm});
            skLineSegment(sketch, "E5.3.1.4", {"start": v(-29.99, -22.56) * mm, "end": v(-26.99, -24.29) * mm});
            skLineSegment(sketch, "E5.3.1.5", {"start": v(-32.99, -24.29) * mm, "end": v(-29.99, -22.56) * mm});
            skLineSegment(sketch, "E5.3.1.6", {"start": v(-26.99, -24.29) * mm, "end": v(-26.99, -27.75) * mm});
            skLineSegment(sketch, "E5.3.1.7", {"start": v(-26.99, -27.75) * mm, "end": v(-29.99, -29.49) * mm});
            skLineSegment(sketch, "E5.3.2.0", {"start": v(-29.2, -21.28) * mm, "end": v(-29.2, -17.81) * mm});
            skCircle(sketch, "E5.3.2.1", {"center": v(-26.2, -19.55) * mm, "radius": 3 * mm, "construction": true});
            skPoint(sketch, "E5.3.2.2", {"position": v(-24.7, -22.14) * mm});
            skLineSegment(sketch, "E5.3.2.3", {"start": v(-26.2, -23) * mm, "end": v(-29.2, -21.28) * mm});
            skLineSegment(sketch, "E5.3.2.4", {"start": v(-26.2, -16.08) * mm, "end": v(-23.2, -17.81) * mm});
            skLineSegment(sketch, "E5.3.2.5", {"start": v(-29.2, -17.81) * mm, "end": v(-26.2, -16.08) * mm});
            skLineSegment(sketch, "E5.3.2.6", {"start": v(-23.2, -17.81) * mm, "end": v(-23.2, -21.28) * mm});
            skLineSegment(sketch, "E5.3.2.7", {"start": v(-23.2, -21.28) * mm, "end": v(-26.2, -23) * mm});
            skLineSegment(sketch, "E5.3.3.0", {"start": v(-25.42, -14.8) * mm, "end": v(-25.42, -11.34) * mm});
            skCircle(sketch, "E5.3.3.1", {"center": v(-22.42, -13.07) * mm, "radius": 3 * mm, "construction": true});
            skPoint(sketch, "E5.3.3.2", {"position": v(-20.92, -15.67) * mm});
            skLineSegment(sketch, "E5.3.3.3", {"start": v(-22.42, -16.53) * mm, "end": v(-25.42, -14.8) * mm});
            skLineSegment(sketch, "E5.3.3.4", {"start": v(-22.42, -9.6) * mm, "end": v(-19.42, -11.34) * mm});
            skLineSegment(sketch, "E5.3.3.5", {"start": v(-25.42, -11.34) * mm, "end": v(-22.42, -9.6) * mm});
            skLineSegment(sketch, "E5.3.3.6", {"start": v(-19.42, -11.34) * mm, "end": v(-19.42, -14.8) * mm});
            skLineSegment(sketch, "E5.3.3.7", {"start": v(-19.42, -14.8) * mm, "end": v(-22.42, -16.53) * mm});
            skLineSegment(sketch, "E5.3.4.0", {"start": v(-21.64, -8.33) * mm, "end": v(-21.64, -4.86) * mm});
            skCircle(sketch, "E5.3.4.1", {"center": v(-18.64, -6.6) * mm, "radius": 3 * mm, "construction": true});
            skPoint(sketch, "E5.3.4.2", {"position": v(-17.14, -9.2) * mm});
            skLineSegment(sketch, "E5.3.4.3", {"start": v(-18.64, -10.06) * mm, "end": v(-21.64, -8.33) * mm});
            skLineSegment(sketch, "E5.3.4.4", {"start": v(-18.64, -3.13) * mm, "end": v(-15.64, -4.86) * mm});
            skLineSegment(sketch, "E5.3.4.5", {"start": v(-21.64, -4.86) * mm, "end": v(-18.64, -3.13) * mm});
            skLineSegment(sketch, "E5.3.4.6", {"start": v(-15.64, -4.86) * mm, "end": v(-15.64, -8.33) * mm});
            skLineSegment(sketch, "E5.3.4.7", {"start": v(-15.64, -8.33) * mm, "end": v(-18.64, -10.06) * mm});
            skLineSegment(sketch, "E5.3.5.0", {"start": v(-17.85, -1.85) * mm, "end": v(-17.85, 1.62) * mm});
            skCircle(sketch, "E5.3.5.1", {"center": v(-14.85, -0.12) * mm, "radius": 3 * mm, "construction": true});
            skPoint(sketch, "E5.3.5.2", {"position": v(-13.35, -2.72) * mm});
            skLineSegment(sketch, "E5.3.5.3", {"start": v(-14.85, -3.58) * mm, "end": v(-17.85, -1.85) * mm});
            skLineSegment(sketch, "E5.3.5.4", {"start": v(-14.85, 3.35) * mm, "end": v(-11.85, 1.62) * mm});
            skLineSegment(sketch, "E5.3.5.5", {"start": v(-17.85, 1.62) * mm, "end": v(-14.85, 3.35) * mm});
            skLineSegment(sketch, "E5.3.5.6", {"start": v(-11.85, 1.62) * mm, "end": v(-11.85, -1.85) * mm});
            skLineSegment(sketch, "E5.3.5.7", {"start": v(-11.85, -1.85) * mm, "end": v(-14.85, -3.58) * mm});
            skLineSegment(sketch, "E5.3.6.0", {"start": v(-14.07, 4.63) * mm, "end": v(-14.07, 8.1) * mm});
            skCircle(sketch, "E5.3.6.1", {"center": v(-11.07, 6.36) * mm, "radius": 3 * mm, "construction": true});
            skPoint(sketch, "E5.3.6.2", {"position": v(-9.57, 3.76) * mm});
            skLineSegment(sketch, "E5.3.6.3", {"start": v(-11.07, 2.9) * mm, "end": v(-14.07, 4.63) * mm});
            skLineSegment(sketch, "E5.3.6.4", {"start": v(-11.07, 9.82) * mm, "end": v(-8.07, 8.1) * mm});
            skLineSegment(sketch, "E5.3.6.5", {"start": v(-14.07, 8.1) * mm, "end": v(-11.07, 9.82) * mm});
            skLineSegment(sketch, "E5.3.6.6", {"start": v(-8.07, 8.1) * mm, "end": v(-8.07, 4.63) * mm});
            skLineSegment(sketch, "E5.3.6.7", {"start": v(-8.07, 4.63) * mm, "end": v(-11.07, 2.9) * mm});
            skLineSegment(sketch, "E5.3.7.0", {"start": v(-10.29, 11.1) * mm, "end": v(-10.29, 14.57) * mm});
            skCircle(sketch, "E5.3.7.1", {"center": v(-7.29, 12.84) * mm, "radius": 3 * mm, "construction": true});
            skPoint(sketch, "E5.3.7.2", {"position": v(-5.79, 10.24) * mm});
            skLineSegment(sketch, "E5.3.7.3", {"start": v(-7.29, 9.37) * mm, "end": v(-10.29, 11.1) * mm});
            skLineSegment(sketch, "E5.3.7.4", {"start": v(-7.29, 16.3) * mm, "end": v(-4.29, 14.57) * mm});
            skLineSegment(sketch, "E5.3.7.5", {"start": v(-10.29, 14.57) * mm, "end": v(-7.29, 16.3) * mm});
            skLineSegment(sketch, "E5.3.7.6", {"start": v(-4.29, 14.57) * mm, "end": v(-4.29, 11.1) * mm});
            skLineSegment(sketch, "E5.3.7.7", {"start": v(-4.29, 11.1) * mm, "end": v(-7.29, 9.37) * mm});
            skLineSegment(sketch, "E5.3.8.0", {"start": v(-6.5, 17.58) * mm, "end": v(-6.5, 21.04) * mm});
            skCircle(sketch, "E5.3.8.1", {"center": v(-3.5, 19.31) * mm, "radius": 3 * mm, "construction": true});
            skPoint(sketch, "E5.3.8.2", {"position": v(-2, 16.71) * mm});
            skLineSegment(sketch, "E5.3.8.3", {"start": v(-3.5, 15.85) * mm, "end": v(-6.5, 17.58) * mm});
            skLineSegment(sketch, "E5.3.8.4", {"start": v(-3.5, 22.78) * mm, "end": v(-0.5, 21.04) * mm});
            skLineSegment(sketch, "E5.3.8.5", {"start": v(-6.5, 21.04) * mm, "end": v(-3.5, 22.78) * mm});
            skLineSegment(sketch, "E5.3.8.6", {"start": v(-0.5, 21.04) * mm, "end": v(-0.5, 17.58) * mm});
            skLineSegment(sketch, "E5.3.8.7", {"start": v(-0.5, 17.58) * mm, "end": v(-3.5, 15.85) * mm});
            skLineSegment(sketch, "E5.3.9.0", {"start": v(-2.72, 24.06) * mm, "end": v(-2.72, 27.52) * mm});
            skCircle(sketch, "E5.3.9.1", {"center": v(0.28, 25.79) * mm, "radius": 3 * mm, "construction": true});
            skPoint(sketch, "E5.3.9.2", {"position": v(1.78, 23.19) * mm});
            skLineSegment(sketch, "E5.3.9.3", {"start": v(0.28, 22.32) * mm, "end": v(-2.72, 24.06) * mm});
            skLineSegment(sketch, "E5.3.9.4", {"start": v(0.28, 29.25) * mm, "end": v(3.28, 27.52) * mm});
            skLineSegment(sketch, "E5.3.9.5", {"start": v(-2.72, 27.52) * mm, "end": v(0.28, 29.25) * mm});
            skLineSegment(sketch, "E5.3.9.6", {"start": v(3.28, 27.52) * mm, "end": v(3.28, 24.06) * mm});
            skLineSegment(sketch, "E5.3.9.7", {"start": v(3.28, 24.06) * mm, "end": v(0.28, 22.32) * mm});
            skLineSegment(sketch, "E5.4.0.0", {"start": v(-29.27, -34.23) * mm, "end": v(-29.27, -30.77) * mm});
            skCircle(sketch, "E5.4.0.1", {"center": v(-26.27, -32.5) * mm, "radius": 3 * mm, "construction": true});
            skPoint(sketch, "E5.4.0.2", {"position": v(-24.77, -35.1) * mm});
            skLineSegment(sketch, "E5.4.0.3", {"start": v(-26.27, -35.96) * mm, "end": v(-29.27, -34.23) * mm});
            skLineSegment(sketch, "E5.4.0.4", {"start": v(-26.27, -29.03) * mm, "end": v(-23.27, -30.77) * mm});
            skLineSegment(sketch, "E5.4.0.5", {"start": v(-29.27, -30.77) * mm, "end": v(-26.27, -29.03) * mm});
            skLineSegment(sketch, "E5.4.0.6", {"start": v(-23.27, -30.77) * mm, "end": v(-23.27, -34.23) * mm});
            skLineSegment(sketch, "E5.4.0.7", {"start": v(-23.27, -34.23) * mm, "end": v(-26.27, -35.96) * mm});
            skLineSegment(sketch, "E5.4.1.0", {"start": v(-25.49, -27.75) * mm, "end": v(-25.49, -24.29) * mm});
            skCircle(sketch, "E5.4.1.1", {"center": v(-22.49, -26.02) * mm, "radius": 3 * mm, "construction": true});
            skPoint(sketch, "E5.4.1.2", {"position": v(-20.99, -28.62) * mm});
            skLineSegment(sketch, "E5.4.1.3", {"start": v(-22.49, -29.49) * mm, "end": v(-25.49, -27.75) * mm});
            skLineSegment(sketch, "E5.4.1.4", {"start": v(-22.49, -22.56) * mm, "end": v(-19.49, -24.29) * mm});
            skLineSegment(sketch, "E5.4.1.5", {"start": v(-25.49, -24.29) * mm, "end": v(-22.49, -22.56) * mm});
            skLineSegment(sketch, "E5.4.1.6", {"start": v(-19.49, -24.29) * mm, "end": v(-19.49, -27.75) * mm});
            skLineSegment(sketch, "E5.4.1.7", {"start": v(-19.49, -27.75) * mm, "end": v(-22.49, -29.49) * mm});
            skLineSegment(sketch, "E5.4.2.0", {"start": v(-21.7, -21.28) * mm, "end": v(-21.7, -17.81) * mm});
            skCircle(sketch, "E5.4.2.1", {"center": v(-18.7, -19.55) * mm, "radius": 3 * mm, "construction": true});
            skPoint(sketch, "E5.4.2.2", {"position": v(-17.2, -22.14) * mm});
            skLineSegment(sketch, "E5.4.2.3", {"start": v(-18.7, -23) * mm, "end": v(-21.7, -21.28) * mm});
            skLineSegment(sketch, "E5.4.2.4", {"start": v(-18.7, -16.08) * mm, "end": v(-15.7, -17.81) * mm});
            skLineSegment(sketch, "E5.4.2.5", {"start": v(-21.7, -17.81) * mm, "end": v(-18.7, -16.08) * mm});
            skLineSegment(sketch, "E5.4.2.6", {"start": v(-15.7, -17.81) * mm, "end": v(-15.7, -21.28) * mm});
            skLineSegment(sketch, "E5.4.2.7", {"start": v(-15.7, -21.28) * mm, "end": v(-18.7, -23) * mm});
            skLineSegment(sketch, "E5.4.3.0", {"start": v(-17.92, -14.8) * mm, "end": v(-17.92, -11.34) * mm});
            skCircle(sketch, "E5.4.3.1", {"center": v(-14.92, -13.07) * mm, "radius": 3 * mm, "construction": true});
            skPoint(sketch, "E5.4.3.2", {"position": v(-13.42, -15.67) * mm});
            skLineSegment(sketch, "E5.4.3.3", {"start": v(-14.92, -16.53) * mm, "end": v(-17.92, -14.8) * mm});
            skLineSegment(sketch, "E5.4.3.4", {"start": v(-14.92, -9.6) * mm, "end": v(-11.92, -11.34) * mm});
            skLineSegment(sketch, "E5.4.3.5", {"start": v(-17.92, -11.34) * mm, "end": v(-14.92, -9.6) * mm});
            skLineSegment(sketch, "E5.4.3.6", {"start": v(-11.92, -11.34) * mm, "end": v(-11.92, -14.8) * mm});
            skLineSegment(sketch, "E5.4.3.7", {"start": v(-11.92, -14.8) * mm, "end": v(-14.92, -16.53) * mm});
            skLineSegment(sketch, "E5.4.4.0", {"start": v(-14.14, -8.33) * mm, "end": v(-14.14, -4.86) * mm});
            skCircle(sketch, "E5.4.4.1", {"center": v(-11.14, -6.6) * mm, "radius": 3 * mm, "construction": true});
            skPoint(sketch, "E5.4.4.2", {"position": v(-9.64, -9.2) * mm});
            skLineSegment(sketch, "E5.4.4.3", {"start": v(-11.14, -10.06) * mm, "end": v(-14.14, -8.33) * mm});
            skLineSegment(sketch, "E5.4.4.4", {"start": v(-11.14, -3.13) * mm, "end": v(-8.14, -4.86) * mm});
            skLineSegment(sketch, "E5.4.4.5", {"start": v(-14.14, -4.86) * mm, "end": v(-11.14, -3.13) * mm});
            skLineSegment(sketch, "E5.4.4.6", {"start": v(-8.14, -4.86) * mm, "end": v(-8.14, -8.33) * mm});
            skLineSegment(sketch, "E5.4.4.7", {"start": v(-8.14, -8.33) * mm, "end": v(-11.14, -10.06) * mm});
            skLineSegment(sketch, "E5.4.5.0", {"start": v(-10.35, -1.85) * mm, "end": v(-10.35, 1.62) * mm});
            skCircle(sketch, "E5.4.5.1", {"center": v(-7.35, -0.12) * mm, "radius": 3 * mm, "construction": true});
            skPoint(sketch, "E5.4.5.2", {"position": v(-5.85, -2.72) * mm});
            skLineSegment(sketch, "E5.4.5.3", {"start": v(-7.35, -3.58) * mm, "end": v(-10.35, -1.85) * mm});
            skLineSegment(sketch, "E5.4.5.4", {"start": v(-7.35, 3.35) * mm, "end": v(-4.35, 1.62) * mm});
            skLineSegment(sketch, "E5.4.5.5", {"start": v(-10.35, 1.62) * mm, "end": v(-7.35, 3.35) * mm});
            skLineSegment(sketch, "E5.4.5.6", {"start": v(-4.35, 1.62) * mm, "end": v(-4.35, -1.85) * mm});
            skLineSegment(sketch, "E5.4.5.7", {"start": v(-4.35, -1.85) * mm, "end": v(-7.35, -3.58) * mm});
            skLineSegment(sketch, "E5.4.6.0", {"start": v(-6.57, 4.63) * mm, "end": v(-6.57, 8.1) * mm});
            skCircle(sketch, "E5.4.6.1", {"center": v(-3.57, 6.36) * mm, "radius": 3 * mm, "construction": true});
            skPoint(sketch, "E5.4.6.2", {"position": v(-2.07, 3.76) * mm});
            skLineSegment(sketch, "E5.4.6.3", {"start": v(-3.57, 2.9) * mm, "end": v(-6.57, 4.63) * mm});
            skLineSegment(sketch, "E5.4.6.4", {"start": v(-3.57, 9.82) * mm, "end": v(-0.57, 8.1) * mm});
            skLineSegment(sketch, "E5.4.6.5", {"start": v(-6.57, 8.1) * mm, "end": v(-3.57, 9.82) * mm});
            skLineSegment(sketch, "E5.4.6.6", {"start": v(-0.57, 8.1) * mm, "end": v(-0.57, 4.63) * mm});
            skLineSegment(sketch, "E5.4.6.7", {"start": v(-0.57, 4.63) * mm, "end": v(-3.57, 2.9) * mm});
            skLineSegment(sketch, "E5.4.7.0", {"start": v(-2.79, 11.1) * mm, "end": v(-2.79, 14.57) * mm});
            skCircle(sketch, "E5.4.7.1", {"center": v(0.21, 12.84) * mm, "radius": 3 * mm, "construction": true});
            skPoint(sketch, "E5.4.7.2", {"position": v(1.71, 10.24) * mm});
            skLineSegment(sketch, "E5.4.7.3", {"start": v(0.21, 9.37) * mm, "end": v(-2.79, 11.1) * mm});
            skLineSegment(sketch, "E5.4.7.4", {"start": v(0.21, 16.3) * mm, "end": v(3.21, 14.57) * mm});
            skLineSegment(sketch, "E5.4.7.5", {"start": v(-2.79, 14.57) * mm, "end": v(0.21, 16.3) * mm});
            skLineSegment(sketch, "E5.4.7.6", {"start": v(3.21, 14.57) * mm, "end": v(3.21, 11.1) * mm});
            skLineSegment(sketch, "E5.4.7.7", {"start": v(3.21, 11.1) * mm, "end": v(0.21, 9.37) * mm});
            skLineSegment(sketch, "E5.4.8.0", {"start": v(1, 17.58) * mm, "end": v(1, 21.04) * mm});
            skCircle(sketch, "E5.4.8.1", {"center": v(4, 19.31) * mm, "radius": 3 * mm, "construction": true});
            skPoint(sketch, "E5.4.8.2", {"position": v(5.5, 16.71) * mm});
            skLineSegment(sketch, "E5.4.8.3", {"start": v(4, 15.85) * mm, "end": v(1, 17.58) * mm});
            skLineSegment(sketch, "E5.4.8.4", {"start": v(4, 22.78) * mm, "end": v(7, 21.04) * mm});
            skLineSegment(sketch, "E5.4.8.5", {"start": v(1, 21.04) * mm, "end": v(4, 22.78) * mm});
            skLineSegment(sketch, "E5.4.8.6", {"start": v(7, 21.04) * mm, "end": v(7, 17.58) * mm});
            skLineSegment(sketch, "E5.4.8.7", {"start": v(7, 17.58) * mm, "end": v(4, 15.85) * mm});
            skLineSegment(sketch, "E5.4.9.0", {"start": v(4.78, 24.06) * mm, "end": v(4.78, 27.52) * mm});
            skCircle(sketch, "E5.4.9.1", {"center": v(7.78, 25.79) * mm, "radius": 3 * mm, "construction": true});
            skPoint(sketch, "E5.4.9.2", {"position": v(9.28, 23.19) * mm});
            skLineSegment(sketch, "E5.4.9.3", {"start": v(7.78, 22.32) * mm, "end": v(4.78, 24.06) * mm});
            skLineSegment(sketch, "E5.4.9.4", {"start": v(7.78, 29.25) * mm, "end": v(10.78, 27.52) * mm});
            skLineSegment(sketch, "E5.4.9.5", {"start": v(4.78, 27.52) * mm, "end": v(7.78, 29.25) * mm});
            skLineSegment(sketch, "E5.4.9.6", {"start": v(10.78, 27.52) * mm, "end": v(10.78, 24.06) * mm});
            skLineSegment(sketch, "E5.4.9.7", {"start": v(10.78, 24.06) * mm, "end": v(7.78, 22.32) * mm});
            skLineSegment(sketch, "E5.5.0.0", {"start": v(-21.77, -34.23) * mm, "end": v(-21.77, -30.77) * mm});
            skCircle(sketch, "E5.5.0.1", {"center": v(-18.77, -32.5) * mm, "radius": 3 * mm, "construction": true});
            skPoint(sketch, "E5.5.0.2", {"position": v(-17.27, -35.1) * mm});
            skLineSegment(sketch, "E5.5.0.3", {"start": v(-18.77, -35.96) * mm, "end": v(-21.77, -34.23) * mm});
            skLineSegment(sketch, "E5.5.0.4", {"start": v(-18.77, -29.03) * mm, "end": v(-15.77, -30.77) * mm});
            skLineSegment(sketch, "E5.5.0.5", {"start": v(-21.77, -30.77) * mm, "end": v(-18.77, -29.03) * mm});
            skLineSegment(sketch, "E5.5.0.6", {"start": v(-15.77, -30.77) * mm, "end": v(-15.77, -34.23) * mm});
            skLineSegment(sketch, "E5.5.0.7", {"start": v(-15.77, -34.23) * mm, "end": v(-18.77, -35.96) * mm});
            skLineSegment(sketch, "E5.5.1.0", {"start": v(-17.99, -27.75) * mm, "end": v(-17.99, -24.29) * mm});
            skCircle(sketch, "E5.5.1.1", {"center": v(-14.99, -26.02) * mm, "radius": 3 * mm, "construction": true});
            skPoint(sketch, "E5.5.1.2", {"position": v(-13.49, -28.62) * mm});
            skLineSegment(sketch, "E5.5.1.3", {"start": v(-14.99, -29.49) * mm, "end": v(-17.99, -27.75) * mm});
            skLineSegment(sketch, "E5.5.1.4", {"start": v(-14.99, -22.56) * mm, "end": v(-11.99, -24.29) * mm});
            skLineSegment(sketch, "E5.5.1.5", {"start": v(-17.99, -24.29) * mm, "end": v(-14.99, -22.56) * mm});
            skLineSegment(sketch, "E5.5.1.6", {"start": v(-11.99, -24.29) * mm, "end": v(-11.99, -27.75) * mm});
            skLineSegment(sketch, "E5.5.1.7", {"start": v(-11.99, -27.75) * mm, "end": v(-14.99, -29.49) * mm});
            skLineSegment(sketch, "E5.5.2.0", {"start": v(-14.2, -21.28) * mm, "end": v(-14.2, -17.81) * mm});
            skCircle(sketch, "E5.5.2.1", {"center": v(-11.2, -19.55) * mm, "radius": 3 * mm, "construction": true});
            skPoint(sketch, "E5.5.2.2", {"position": v(-9.7, -22.14) * mm});
            skLineSegment(sketch, "E5.5.2.3", {"start": v(-11.2, -23) * mm, "end": v(-14.2, -21.28) * mm});
            skLineSegment(sketch, "E5.5.2.4", {"start": v(-11.2, -16.08) * mm, "end": v(-8.2, -17.81) * mm});
            skLineSegment(sketch, "E5.5.2.5", {"start": v(-14.2, -17.81) * mm, "end": v(-11.2, -16.08) * mm});
            skLineSegment(sketch, "E5.5.2.6", {"start": v(-8.2, -17.81) * mm, "end": v(-8.2, -21.28) * mm});
            skLineSegment(sketch, "E5.5.2.7", {"start": v(-8.2, -21.28) * mm, "end": v(-11.2, -23) * mm});
            skLineSegment(sketch, "E5.5.3.0", {"start": v(-10.42, -14.8) * mm, "end": v(-10.42, -11.34) * mm});
            skCircle(sketch, "E5.5.3.1", {"center": v(-7.42, -13.07) * mm, "radius": 3 * mm, "construction": true});
            skPoint(sketch, "E5.5.3.2", {"position": v(-5.92, -15.67) * mm});
            skLineSegment(sketch, "E5.5.3.3", {"start": v(-7.42, -16.53) * mm, "end": v(-10.42, -14.8) * mm});
            skLineSegment(sketch, "E5.5.3.4", {"start": v(-7.42, -9.6) * mm, "end": v(-4.42, -11.34) * mm});
            skLineSegment(sketch, "E5.5.3.5", {"start": v(-10.42, -11.34) * mm, "end": v(-7.42, -9.6) * mm});
            skLineSegment(sketch, "E5.5.3.6", {"start": v(-4.42, -11.34) * mm, "end": v(-4.42, -14.8) * mm});
            skLineSegment(sketch, "E5.5.3.7", {"start": v(-4.42, -14.8) * mm, "end": v(-7.42, -16.53) * mm});
            skLineSegment(sketch, "E5.5.4.0", {"start": v(-6.64, -8.33) * mm, "end": v(-6.64, -4.86) * mm});
            skCircle(sketch, "E5.5.4.1", {"center": v(-3.64, -6.6) * mm, "radius": 3 * mm, "construction": true});
            skPoint(sketch, "E5.5.4.2", {"position": v(-2.14, -9.2) * mm});
            skLineSegment(sketch, "E5.5.4.3", {"start": v(-3.64, -10.06) * mm, "end": v(-6.64, -8.33) * mm});
            skLineSegment(sketch, "E5.5.4.4", {"start": v(-3.64, -3.13) * mm, "end": v(-0.64, -4.86) * mm});
            skLineSegment(sketch, "E5.5.4.5", {"start": v(-6.64, -4.86) * mm, "end": v(-3.64, -3.13) * mm});
            skLineSegment(sketch, "E5.5.4.6", {"start": v(-0.64, -4.86) * mm, "end": v(-0.64, -8.33) * mm});
            skLineSegment(sketch, "E5.5.4.7", {"start": v(-0.64, -8.33) * mm, "end": v(-3.64, -10.06) * mm});
            skLineSegment(sketch, "E5.5.5.0", {"start": v(-2.85, -1.85) * mm, "end": v(-2.85, 1.62) * mm});
            skCircle(sketch, "E5.5.5.1", {"center": v(0.15, -0.12) * mm, "radius": 3 * mm, "construction": true});
            skPoint(sketch, "E5.5.5.2", {"position": v(1.65, -2.72) * mm});
            skLineSegment(sketch, "E5.5.5.3", {"start": v(0.15, -3.58) * mm, "end": v(-2.85, -1.85) * mm});
            skLineSegment(sketch, "E5.5.5.4", {"start": v(0.15, 3.35) * mm, "end": v(3.15, 1.62) * mm});
            skLineSegment(sketch, "E5.5.5.5", {"start": v(-2.85, 1.62) * mm, "end": v(0.15, 3.35) * mm});
            skLineSegment(sketch, "E5.5.5.6", {"start": v(3.15, 1.62) * mm, "end": v(3.15, -1.85) * mm});
            skLineSegment(sketch, "E5.5.5.7", {"start": v(3.15, -1.85) * mm, "end": v(0.15, -3.58) * mm});
            skLineSegment(sketch, "E5.5.6.0", {"start": v(0.93, 4.63) * mm, "end": v(0.93, 8.1) * mm});
            skCircle(sketch, "E5.5.6.1", {"center": v(3.93, 6.36) * mm, "radius": 3 * mm, "construction": true});
            skPoint(sketch, "E5.5.6.2", {"position": v(5.43, 3.76) * mm});
            skLineSegment(sketch, "E5.5.6.3", {"start": v(3.93, 2.9) * mm, "end": v(0.93, 4.63) * mm});
            skLineSegment(sketch, "E5.5.6.4", {"start": v(3.93, 9.82) * mm, "end": v(6.93, 8.1) * mm});
            skLineSegment(sketch, "E5.5.6.5", {"start": v(0.93, 8.1) * mm, "end": v(3.93, 9.82) * mm});
            skLineSegment(sketch, "E5.5.6.6", {"start": v(6.93, 8.1) * mm, "end": v(6.93, 4.63) * mm});
            skLineSegment(sketch, "E5.5.6.7", {"start": v(6.93, 4.63) * mm, "end": v(3.93, 2.9) * mm});
            skLineSegment(sketch, "E5.5.7.0", {"start": v(4.71, 11.1) * mm, "end": v(4.71, 14.57) * mm});
            skCircle(sketch, "E5.5.7.1", {"center": v(7.71, 12.84) * mm, "radius": 3 * mm, "construction": true});
            skPoint(sketch, "E5.5.7.2", {"position": v(9.21, 10.24) * mm});
            skLineSegment(sketch, "E5.5.7.3", {"start": v(7.71, 9.37) * mm, "end": v(4.71, 11.1) * mm});
            skLineSegment(sketch, "E5.5.7.4", {"start": v(7.71, 16.3) * mm, "end": v(10.71, 14.57) * mm});
            skLineSegment(sketch, "E5.5.7.5", {"start": v(4.71, 14.57) * mm, "end": v(7.71, 16.3) * mm});
            skLineSegment(sketch, "E5.5.7.6", {"start": v(10.71, 14.57) * mm, "end": v(10.71, 11.1) * mm});
            skLineSegment(sketch, "E5.5.7.7", {"start": v(10.71, 11.1) * mm, "end": v(7.71, 9.37) * mm});
            skLineSegment(sketch, "E5.5.8.0", {"start": v(8.5, 17.58) * mm, "end": v(8.5, 21.04) * mm});
            skCircle(sketch, "E5.5.8.1", {"center": v(11.5, 19.31) * mm, "radius": 3 * mm, "construction": true});
            skPoint(sketch, "E5.5.8.2", {"position": v(13, 16.71) * mm});
            skLineSegment(sketch, "E5.5.8.3", {"start": v(11.5, 15.85) * mm, "end": v(8.5, 17.58) * mm});
            skLineSegment(sketch, "E5.5.8.4", {"start": v(11.5, 22.78) * mm, "end": v(14.5, 21.04) * mm});
            skLineSegment(sketch, "E5.5.8.5", {"start": v(8.5, 21.04) * mm, "end": v(11.5, 22.78) * mm});
            skLineSegment(sketch, "E5.5.8.6", {"start": v(14.5, 21.04) * mm, "end": v(14.5, 17.58) * mm});
            skLineSegment(sketch, "E5.5.8.7", {"start": v(14.5, 17.58) * mm, "end": v(11.5, 15.85) * mm});
            skLineSegment(sketch, "E5.5.9.0", {"start": v(12.28, 24.06) * mm, "end": v(12.28, 27.52) * mm});
            skCircle(sketch, "E5.5.9.1", {"center": v(15.28, 25.79) * mm, "radius": 3 * mm, "construction": true});
            skPoint(sketch, "E5.5.9.2", {"position": v(16.78, 23.19) * mm});
            skLineSegment(sketch, "E5.5.9.3", {"start": v(15.28, 22.32) * mm, "end": v(12.28, 24.06) * mm});
            skLineSegment(sketch, "E5.5.9.4", {"start": v(15.28, 29.25) * mm, "end": v(18.28, 27.52) * mm});
            skLineSegment(sketch, "E5.5.9.5", {"start": v(12.28, 27.52) * mm, "end": v(15.28, 29.25) * mm});
            skLineSegment(sketch, "E5.5.9.6", {"start": v(18.28, 27.52) * mm, "end": v(18.28, 24.06) * mm});
            skLineSegment(sketch, "E5.5.9.7", {"start": v(18.28, 24.06) * mm, "end": v(15.28, 22.32) * mm});
            skLineSegment(sketch, "E5.6.0.0", {"start": v(-14.27, -34.23) * mm, "end": v(-14.27, -30.77) * mm});
            skCircle(sketch, "E5.6.0.1", {"center": v(-11.27, -32.5) * mm, "radius": 3 * mm, "construction": true});
            skPoint(sketch, "E5.6.0.2", {"position": v(-9.77, -35.1) * mm});
            skLineSegment(sketch, "E5.6.0.3", {"start": v(-11.27, -35.96) * mm, "end": v(-14.27, -34.23) * mm});
            skLineSegment(sketch, "E5.6.0.4", {"start": v(-11.27, -29.03) * mm, "end": v(-8.27, -30.77) * mm});
            skLineSegment(sketch, "E5.6.0.5", {"start": v(-14.27, -30.77) * mm, "end": v(-11.27, -29.03) * mm});
            skLineSegment(sketch, "E5.6.0.6", {"start": v(-8.27, -30.77) * mm, "end": v(-8.27, -34.23) * mm});
            skLineSegment(sketch, "E5.6.0.7", {"start": v(-8.27, -34.23) * mm, "end": v(-11.27, -35.96) * mm});
            skLineSegment(sketch, "E5.6.1.0", {"start": v(-10.49, -27.75) * mm, "end": v(-10.49, -24.29) * mm});
            skCircle(sketch, "E5.6.1.1", {"center": v(-7.49, -26.02) * mm, "radius": 3 * mm, "construction": true});
            skPoint(sketch, "E5.6.1.2", {"position": v(-5.99, -28.62) * mm});
            skLineSegment(sketch, "E5.6.1.3", {"start": v(-7.49, -29.49) * mm, "end": v(-10.49, -27.75) * mm});
            skLineSegment(sketch, "E5.6.1.4", {"start": v(-7.49, -22.56) * mm, "end": v(-4.49, -24.29) * mm});
            skLineSegment(sketch, "E5.6.1.5", {"start": v(-10.49, -24.29) * mm, "end": v(-7.49, -22.56) * mm});
            skLineSegment(sketch, "E5.6.1.6", {"start": v(-4.49, -24.29) * mm, "end": v(-4.49, -27.75) * mm});
            skLineSegment(sketch, "E5.6.1.7", {"start": v(-4.49, -27.75) * mm, "end": v(-7.49, -29.49) * mm});
            skLineSegment(sketch, "E5.6.2.0", {"start": v(-6.7, -21.28) * mm, "end": v(-6.7, -17.81) * mm});
            skCircle(sketch, "E5.6.2.1", {"center": v(-3.7, -19.55) * mm, "radius": 3 * mm, "construction": true});
            skPoint(sketch, "E5.6.2.2", {"position": v(-2.2, -22.14) * mm});
            skLineSegment(sketch, "E5.6.2.3", {"start": v(-3.7, -23) * mm, "end": v(-6.7, -21.28) * mm});
            skLineSegment(sketch, "E5.6.2.4", {"start": v(-3.7, -16.08) * mm, "end": v(-0.7, -17.81) * mm});
            skLineSegment(sketch, "E5.6.2.5", {"start": v(-6.7, -17.81) * mm, "end": v(-3.7, -16.08) * mm});
            skLineSegment(sketch, "E5.6.2.6", {"start": v(-0.7, -17.81) * mm, "end": v(-0.7, -21.28) * mm});
            skLineSegment(sketch, "E5.6.2.7", {"start": v(-0.7, -21.28) * mm, "end": v(-3.7, -23) * mm});
            skLineSegment(sketch, "E5.6.3.0", {"start": v(-2.92, -14.8) * mm, "end": v(-2.92, -11.34) * mm});
            skCircle(sketch, "E5.6.3.1", {"center": v(0.08, -13.07) * mm, "radius": 3 * mm, "construction": true});
            skPoint(sketch, "E5.6.3.2", {"position": v(1.58, -15.67) * mm});
            skLineSegment(sketch, "E5.6.3.3", {"start": v(0.08, -16.53) * mm, "end": v(-2.92, -14.8) * mm});
            skLineSegment(sketch, "E5.6.3.4", {"start": v(0.08, -9.6) * mm, "end": v(3.08, -11.34) * mm});
            skLineSegment(sketch, "E5.6.3.5", {"start": v(-2.92, -11.34) * mm, "end": v(0.08, -9.6) * mm});
            skLineSegment(sketch, "E5.6.3.6", {"start": v(3.08, -11.34) * mm, "end": v(3.08, -14.8) * mm});
            skLineSegment(sketch, "E5.6.3.7", {"start": v(3.08, -14.8) * mm, "end": v(0.08, -16.53) * mm});
            skLineSegment(sketch, "E5.6.4.0", {"start": v(0.86, -8.33) * mm, "end": v(0.86, -4.86) * mm});
            skCircle(sketch, "E5.6.4.1", {"center": v(3.86, -6.6) * mm, "radius": 3 * mm, "construction": true});
            skPoint(sketch, "E5.6.4.2", {"position": v(5.36, -9.2) * mm});
            skLineSegment(sketch, "E5.6.4.3", {"start": v(3.86, -10.06) * mm, "end": v(0.86, -8.33) * mm});
            skLineSegment(sketch, "E5.6.4.4", {"start": v(3.86, -3.13) * mm, "end": v(6.86, -4.86) * mm});
            skLineSegment(sketch, "E5.6.4.5", {"start": v(0.86, -4.86) * mm, "end": v(3.86, -3.13) * mm});
            skLineSegment(sketch, "E5.6.4.6", {"start": v(6.86, -4.86) * mm, "end": v(6.86, -8.33) * mm});
            skLineSegment(sketch, "E5.6.4.7", {"start": v(6.86, -8.33) * mm, "end": v(3.86, -10.06) * mm});
            skLineSegment(sketch, "E5.6.5.0", {"start": v(4.65, -1.85) * mm, "end": v(4.65, 1.62) * mm});
            skCircle(sketch, "E5.6.5.1", {"center": v(7.65, -0.12) * mm, "radius": 3 * mm, "construction": true});
            skPoint(sketch, "E5.6.5.2", {"position": v(9.15, -2.72) * mm});
            skLineSegment(sketch, "E5.6.5.3", {"start": v(7.65, -3.58) * mm, "end": v(4.65, -1.85) * mm});
            skLineSegment(sketch, "E5.6.5.4", {"start": v(7.65, 3.35) * mm, "end": v(10.65, 1.62) * mm});
            skLineSegment(sketch, "E5.6.5.5", {"start": v(4.65, 1.62) * mm, "end": v(7.65, 3.35) * mm});
            skLineSegment(sketch, "E5.6.5.6", {"start": v(10.65, 1.62) * mm, "end": v(10.65, -1.85) * mm});
            skLineSegment(sketch, "E5.6.5.7", {"start": v(10.65, -1.85) * mm, "end": v(7.65, -3.58) * mm});
            skLineSegment(sketch, "E5.6.6.0", {"start": v(8.43, 4.63) * mm, "end": v(8.43, 8.1) * mm});
            skCircle(sketch, "E5.6.6.1", {"center": v(11.43, 6.36) * mm, "radius": 3 * mm, "construction": true});
            skPoint(sketch, "E5.6.6.2", {"position": v(12.93, 3.76) * mm});
            skLineSegment(sketch, "E5.6.6.3", {"start": v(11.43, 2.9) * mm, "end": v(8.43, 4.63) * mm});
            skLineSegment(sketch, "E5.6.6.4", {"start": v(11.43, 9.82) * mm, "end": v(14.43, 8.1) * mm});
            skLineSegment(sketch, "E5.6.6.5", {"start": v(8.43, 8.1) * mm, "end": v(11.43, 9.82) * mm});
            skLineSegment(sketch, "E5.6.6.6", {"start": v(14.43, 8.1) * mm, "end": v(14.43, 4.63) * mm});
            skLineSegment(sketch, "E5.6.6.7", {"start": v(14.43, 4.63) * mm, "end": v(11.43, 2.9) * mm});
            skLineSegment(sketch, "E5.6.7.0", {"start": v(12.21, 11.1) * mm, "end": v(12.21, 14.57) * mm});
            skCircle(sketch, "E5.6.7.1", {"center": v(15.21, 12.84) * mm, "radius": 3 * mm, "construction": true});
            skPoint(sketch, "E5.6.7.2", {"position": v(16.71, 10.24) * mm});
            skLineSegment(sketch, "E5.6.7.3", {"start": v(15.21, 9.37) * mm, "end": v(12.21, 11.1) * mm});
            skLineSegment(sketch, "E5.6.7.4", {"start": v(15.21, 16.3) * mm, "end": v(18.21, 14.57) * mm});
            skLineSegment(sketch, "E5.6.7.5", {"start": v(12.21, 14.57) * mm, "end": v(15.21, 16.3) * mm});
            skLineSegment(sketch, "E5.6.7.6", {"start": v(18.21, 14.57) * mm, "end": v(18.21, 11.1) * mm});
            skLineSegment(sketch, "E5.6.7.7", {"start": v(18.21, 11.1) * mm, "end": v(15.21, 9.37) * mm});
            skLineSegment(sketch, "E5.6.8.0", {"start": v(16, 17.58) * mm, "end": v(16, 21.04) * mm});
            skCircle(sketch, "E5.6.8.1", {"center": v(19, 19.31) * mm, "radius": 3 * mm, "construction": true});
            skPoint(sketch, "E5.6.8.2", {"position": v(20.5, 16.71) * mm});
            skLineSegment(sketch, "E5.6.8.3", {"start": v(19, 15.85) * mm, "end": v(16, 17.58) * mm});
            skLineSegment(sketch, "E5.6.8.4", {"start": v(19, 22.78) * mm, "end": v(22, 21.04) * mm});
            skLineSegment(sketch, "E5.6.8.5", {"start": v(16, 21.04) * mm, "end": v(19, 22.78) * mm});
            skLineSegment(sketch, "E5.6.8.6", {"start": v(22, 21.04) * mm, "end": v(22, 17.58) * mm});
            skLineSegment(sketch, "E5.6.8.7", {"start": v(22, 17.58) * mm, "end": v(19, 15.85) * mm});
            skLineSegment(sketch, "E5.6.9.0", {"start": v(19.78, 24.06) * mm, "end": v(19.78, 27.52) * mm});
            skCircle(sketch, "E5.6.9.1", {"center": v(22.78, 25.79) * mm, "radius": 3 * mm, "construction": true});
            skPoint(sketch, "E5.6.9.2", {"position": v(24.28, 23.19) * mm});
            skLineSegment(sketch, "E5.6.9.3", {"start": v(22.78, 22.32) * mm, "end": v(19.78, 24.06) * mm});
            skLineSegment(sketch, "E5.6.9.4", {"start": v(22.78, 29.25) * mm, "end": v(25.78, 27.52) * mm});
            skLineSegment(sketch, "E5.6.9.5", {"start": v(19.78, 27.52) * mm, "end": v(22.78, 29.25) * mm});
            skLineSegment(sketch, "E5.6.9.6", {"start": v(25.78, 27.52) * mm, "end": v(25.78, 24.06) * mm});
            skLineSegment(sketch, "E5.6.9.7", {"start": v(25.78, 24.06) * mm, "end": v(22.78, 22.32) * mm});
            skLineSegment(sketch, "E5.7.0.0", {"start": v(-6.77, -34.23) * mm, "end": v(-6.77, -30.77) * mm});
            skCircle(sketch, "E5.7.0.1", {"center": v(-3.77, -32.5) * mm, "radius": 3 * mm, "construction": true});
            skPoint(sketch, "E5.7.0.2", {"position": v(-2.27, -35.1) * mm});
            skLineSegment(sketch, "E5.7.0.3", {"start": v(-3.77, -35.96) * mm, "end": v(-6.77, -34.23) * mm});
            skLineSegment(sketch, "E5.7.0.4", {"start": v(-3.77, -29.03) * mm, "end": v(-0.77, -30.77) * mm});
            skLineSegment(sketch, "E5.7.0.5", {"start": v(-6.77, -30.77) * mm, "end": v(-3.77, -29.03) * mm});
            skLineSegment(sketch, "E5.7.0.6", {"start": v(-0.77, -30.77) * mm, "end": v(-0.77, -34.23) * mm});
            skLineSegment(sketch, "E5.7.0.7", {"start": v(-0.77, -34.23) * mm, "end": v(-3.77, -35.96) * mm});
            skLineSegment(sketch, "E5.7.1.0", {"start": v(-2.99, -27.75) * mm, "end": v(-2.99, -24.29) * mm});
            skCircle(sketch, "E5.7.1.1", {"center": v(0.01, -26.02) * mm, "radius": 3 * mm, "construction": true});
            skPoint(sketch, "E5.7.1.2", {"position": v(1.51, -28.62) * mm});
            skLineSegment(sketch, "E5.7.1.3", {"start": v(0.01, -29.49) * mm, "end": v(-2.99, -27.75) * mm});
            skLineSegment(sketch, "E5.7.1.4", {"start": v(0.01, -22.56) * mm, "end": v(3.01, -24.29) * mm});
            skLineSegment(sketch, "E5.7.1.5", {"start": v(-2.99, -24.29) * mm, "end": v(0.01, -22.56) * mm});
            skLineSegment(sketch, "E5.7.1.6", {"start": v(3.01, -24.29) * mm, "end": v(3.01, -27.75) * mm});
            skLineSegment(sketch, "E5.7.1.7", {"start": v(3.01, -27.75) * mm, "end": v(0.01, -29.49) * mm});
            skLineSegment(sketch, "E5.7.2.0", {"start": v(0.8, -21.28) * mm, "end": v(0.8, -17.81) * mm});
            skCircle(sketch, "E5.7.2.1", {"center": v(3.8, -19.55) * mm, "radius": 3 * mm, "construction": true});
            skPoint(sketch, "E5.7.2.2", {"position": v(5.3, -22.14) * mm});
            skLineSegment(sketch, "E5.7.2.3", {"start": v(3.8, -23) * mm, "end": v(0.8, -21.28) * mm});
            skLineSegment(sketch, "E5.7.2.4", {"start": v(3.8, -16.08) * mm, "end": v(6.8, -17.81) * mm});
            skLineSegment(sketch, "E5.7.2.5", {"start": v(0.8, -17.81) * mm, "end": v(3.8, -16.08) * mm});
            skLineSegment(sketch, "E5.7.2.6", {"start": v(6.8, -17.81) * mm, "end": v(6.8, -21.28) * mm});
            skLineSegment(sketch, "E5.7.2.7", {"start": v(6.8, -21.28) * mm, "end": v(3.8, -23) * mm});
            skLineSegment(sketch, "E5.7.3.0", {"start": v(4.58, -14.8) * mm, "end": v(4.58, -11.34) * mm});
            skCircle(sketch, "E5.7.3.1", {"center": v(7.58, -13.07) * mm, "radius": 3 * mm, "construction": true});
            skPoint(sketch, "E5.7.3.2", {"position": v(9.08, -15.67) * mm});
            skLineSegment(sketch, "E5.7.3.3", {"start": v(7.58, -16.53) * mm, "end": v(4.58, -14.8) * mm});
            skLineSegment(sketch, "E5.7.3.4", {"start": v(7.58, -9.6) * mm, "end": v(10.58, -11.34) * mm});
            skLineSegment(sketch, "E5.7.3.5", {"start": v(4.58, -11.34) * mm, "end": v(7.58, -9.6) * mm});
            skLineSegment(sketch, "E5.7.3.6", {"start": v(10.58, -11.34) * mm, "end": v(10.58, -14.8) * mm});
            skLineSegment(sketch, "E5.7.3.7", {"start": v(10.58, -14.8) * mm, "end": v(7.58, -16.53) * mm});
            skLineSegment(sketch, "E5.7.4.0", {"start": v(8.36, -8.33) * mm, "end": v(8.36, -4.86) * mm});
            skCircle(sketch, "E5.7.4.1", {"center": v(11.36, -6.6) * mm, "radius": 3 * mm, "construction": true});
            skPoint(sketch, "E5.7.4.2", {"position": v(12.86, -9.2) * mm});
            skLineSegment(sketch, "E5.7.4.3", {"start": v(11.36, -10.06) * mm, "end": v(8.36, -8.33) * mm});
            skLineSegment(sketch, "E5.7.4.4", {"start": v(11.36, -3.13) * mm, "end": v(14.36, -4.86) * mm});
            skLineSegment(sketch, "E5.7.4.5", {"start": v(8.36, -4.86) * mm, "end": v(11.36, -3.13) * mm});
            skLineSegment(sketch, "E5.7.4.6", {"start": v(14.36, -4.86) * mm, "end": v(14.36, -8.33) * mm});
            skLineSegment(sketch, "E5.7.4.7", {"start": v(14.36, -8.33) * mm, "end": v(11.36, -10.06) * mm});
            skLineSegment(sketch, "E5.7.5.0", {"start": v(12.15, -1.85) * mm, "end": v(12.15, 1.62) * mm});
            skCircle(sketch, "E5.7.5.1", {"center": v(15.15, -0.12) * mm, "radius": 3 * mm, "construction": true});
            skPoint(sketch, "E5.7.5.2", {"position": v(16.65, -2.72) * mm});
            skLineSegment(sketch, "E5.7.5.3", {"start": v(15.15, -3.58) * mm, "end": v(12.15, -1.85) * mm});
            skLineSegment(sketch, "E5.7.5.4", {"start": v(15.15, 3.35) * mm, "end": v(18.15, 1.62) * mm});
            skLineSegment(sketch, "E5.7.5.5", {"start": v(12.15, 1.62) * mm, "end": v(15.15, 3.35) * mm});
            skLineSegment(sketch, "E5.7.5.6", {"start": v(18.15, 1.62) * mm, "end": v(18.15, -1.85) * mm});
            skLineSegment(sketch, "E5.7.5.7", {"start": v(18.15, -1.85) * mm, "end": v(15.15, -3.58) * mm});
            skLineSegment(sketch, "E5.7.6.0", {"start": v(15.93, 4.63) * mm, "end": v(15.93, 8.1) * mm});
            skCircle(sketch, "E5.7.6.1", {"center": v(18.93, 6.36) * mm, "radius": 3 * mm, "construction": true});
            skPoint(sketch, "E5.7.6.2", {"position": v(20.43, 3.76) * mm});
            skLineSegment(sketch, "E5.7.6.3", {"start": v(18.93, 2.9) * mm, "end": v(15.93, 4.63) * mm});
            skLineSegment(sketch, "E5.7.6.4", {"start": v(18.93, 9.82) * mm, "end": v(21.93, 8.1) * mm});
            skLineSegment(sketch, "E5.7.6.5", {"start": v(15.93, 8.1) * mm, "end": v(18.93, 9.82) * mm});
            skLineSegment(sketch, "E5.7.6.6", {"start": v(21.93, 8.1) * mm, "end": v(21.93, 4.63) * mm});
            skLineSegment(sketch, "E5.7.6.7", {"start": v(21.93, 4.63) * mm, "end": v(18.93, 2.9) * mm});
            skLineSegment(sketch, "E5.7.7.0", {"start": v(19.71, 11.1) * mm, "end": v(19.71, 14.57) * mm});
            skCircle(sketch, "E5.7.7.1", {"center": v(22.71, 12.84) * mm, "radius": 3 * mm, "construction": true});
            skPoint(sketch, "E5.7.7.2", {"position": v(24.21, 10.24) * mm});
            skLineSegment(sketch, "E5.7.7.3", {"start": v(22.71, 9.37) * mm, "end": v(19.71, 11.1) * mm});
            skLineSegment(sketch, "E5.7.7.4", {"start": v(22.71, 16.3) * mm, "end": v(25.71, 14.57) * mm});
            skLineSegment(sketch, "E5.7.7.5", {"start": v(19.71, 14.57) * mm, "end": v(22.71, 16.3) * mm});
            skLineSegment(sketch, "E5.7.7.6", {"start": v(25.71, 14.57) * mm, "end": v(25.71, 11.1) * mm});
            skLineSegment(sketch, "E5.7.7.7", {"start": v(25.71, 11.1) * mm, "end": v(22.71, 9.37) * mm});
            skLineSegment(sketch, "E5.7.8.0", {"start": v(23.5, 17.58) * mm, "end": v(23.5, 21.04) * mm});
            skCircle(sketch, "E5.7.8.1", {"center": v(26.5, 19.31) * mm, "radius": 3 * mm, "construction": true});
            skPoint(sketch, "E5.7.8.2", {"position": v(28, 16.71) * mm});
            skLineSegment(sketch, "E5.7.8.3", {"start": v(26.5, 15.85) * mm, "end": v(23.5, 17.58) * mm});
            skLineSegment(sketch, "E5.7.8.4", {"start": v(26.5, 22.78) * mm, "end": v(29.5, 21.04) * mm});
            skLineSegment(sketch, "E5.7.8.5", {"start": v(23.5, 21.04) * mm, "end": v(26.5, 22.78) * mm});
            skLineSegment(sketch, "E5.7.8.6", {"start": v(29.5, 21.04) * mm, "end": v(29.5, 17.58) * mm});
            skLineSegment(sketch, "E5.7.8.7", {"start": v(29.5, 17.58) * mm, "end": v(26.5, 15.85) * mm});
            skLineSegment(sketch, "E5.7.9.0", {"start": v(27.28, 24.06) * mm, "end": v(27.28, 27.52) * mm});
            skCircle(sketch, "E5.7.9.1", {"center": v(30.28, 25.79) * mm, "radius": 3 * mm, "construction": true});
            skPoint(sketch, "E5.7.9.2", {"position": v(31.78, 23.19) * mm});
            skLineSegment(sketch, "E5.7.9.3", {"start": v(30.28, 22.32) * mm, "end": v(27.28, 24.06) * mm});
            skLineSegment(sketch, "E5.7.9.4", {"start": v(30.28, 29.25) * mm, "end": v(33.28, 27.52) * mm});
            skLineSegment(sketch, "E5.7.9.5", {"start": v(27.28, 27.52) * mm, "end": v(30.28, 29.25) * mm});
            skLineSegment(sketch, "E5.7.9.6", {"start": v(33.28, 27.52) * mm, "end": v(33.28, 24.06) * mm});
            skLineSegment(sketch, "E5.7.9.7", {"start": v(33.28, 24.06) * mm, "end": v(30.28, 22.32) * mm});
            skLineSegment(sketch, "E5.8.0.0", {"start": v(0.73, -34.23) * mm, "end": v(0.73, -30.77) * mm});
            skCircle(sketch, "E5.8.0.1", {"center": v(3.73, -32.5) * mm, "radius": 3 * mm, "construction": true});
            skPoint(sketch, "E5.8.0.2", {"position": v(5.23, -35.1) * mm});
            skLineSegment(sketch, "E5.8.0.3", {"start": v(3.73, -35.96) * mm, "end": v(0.73, -34.23) * mm});
            skLineSegment(sketch, "E5.8.0.4", {"start": v(3.73, -29.03) * mm, "end": v(6.73, -30.77) * mm});
            skLineSegment(sketch, "E5.8.0.5", {"start": v(0.73, -30.77) * mm, "end": v(3.73, -29.03) * mm});
            skLineSegment(sketch, "E5.8.0.6", {"start": v(6.73, -30.77) * mm, "end": v(6.73, -34.23) * mm});
            skLineSegment(sketch, "E5.8.0.7", {"start": v(6.73, -34.23) * mm, "end": v(3.73, -35.96) * mm});
            skLineSegment(sketch, "E5.8.1.0", {"start": v(4.51, -27.75) * mm, "end": v(4.51, -24.29) * mm});
            skCircle(sketch, "E5.8.1.1", {"center": v(7.51, -26.02) * mm, "radius": 3 * mm, "construction": true});
            skPoint(sketch, "E5.8.1.2", {"position": v(9.01, -28.62) * mm});
            skLineSegment(sketch, "E5.8.1.3", {"start": v(7.51, -29.49) * mm, "end": v(4.51, -27.75) * mm});
            skLineSegment(sketch, "E5.8.1.4", {"start": v(7.51, -22.56) * mm, "end": v(10.51, -24.29) * mm});
            skLineSegment(sketch, "E5.8.1.5", {"start": v(4.51, -24.29) * mm, "end": v(7.51, -22.56) * mm});
            skLineSegment(sketch, "E5.8.1.6", {"start": v(10.51, -24.29) * mm, "end": v(10.51, -27.75) * mm});
            skLineSegment(sketch, "E5.8.1.7", {"start": v(10.51, -27.75) * mm, "end": v(7.51, -29.49) * mm});
            skLineSegment(sketch, "E5.8.2.0", {"start": v(8.3, -21.28) * mm, "end": v(8.3, -17.81) * mm});
            skCircle(sketch, "E5.8.2.1", {"center": v(11.3, -19.55) * mm, "radius": 3 * mm, "construction": true});
            skPoint(sketch, "E5.8.2.2", {"position": v(12.8, -22.14) * mm});
            skLineSegment(sketch, "E5.8.2.3", {"start": v(11.3, -23) * mm, "end": v(8.3, -21.28) * mm});
            skLineSegment(sketch, "E5.8.2.4", {"start": v(11.3, -16.08) * mm, "end": v(14.3, -17.81) * mm});
            skLineSegment(sketch, "E5.8.2.5", {"start": v(8.3, -17.81) * mm, "end": v(11.3, -16.08) * mm});
            skLineSegment(sketch, "E5.8.2.6", {"start": v(14.3, -17.81) * mm, "end": v(14.3, -21.28) * mm});
            skLineSegment(sketch, "E5.8.2.7", {"start": v(14.3, -21.28) * mm, "end": v(11.3, -23) * mm});
            skLineSegment(sketch, "E5.8.3.0", {"start": v(12.08, -14.8) * mm, "end": v(12.08, -11.34) * mm});
            skCircle(sketch, "E5.8.3.1", {"center": v(15.08, -13.07) * mm, "radius": 3 * mm, "construction": true});
            skPoint(sketch, "E5.8.3.2", {"position": v(16.58, -15.67) * mm});
            skLineSegment(sketch, "E5.8.3.3", {"start": v(15.08, -16.53) * mm, "end": v(12.08, -14.8) * mm});
            skLineSegment(sketch, "E5.8.3.4", {"start": v(15.08, -9.6) * mm, "end": v(18.08, -11.34) * mm});
            skLineSegment(sketch, "E5.8.3.5", {"start": v(12.08, -11.34) * mm, "end": v(15.08, -9.6) * mm});
            skLineSegment(sketch, "E5.8.3.6", {"start": v(18.08, -11.34) * mm, "end": v(18.08, -14.8) * mm});
            skLineSegment(sketch, "E5.8.3.7", {"start": v(18.08, -14.8) * mm, "end": v(15.08, -16.53) * mm});
            skLineSegment(sketch, "E5.8.4.0", {"start": v(15.86, -8.33) * mm, "end": v(15.86, -4.86) * mm});
            skCircle(sketch, "E5.8.4.1", {"center": v(18.86, -6.6) * mm, "radius": 3 * mm, "construction": true});
            skPoint(sketch, "E5.8.4.2", {"position": v(20.36, -9.2) * mm});
            skLineSegment(sketch, "E5.8.4.3", {"start": v(18.86, -10.06) * mm, "end": v(15.86, -8.33) * mm});
            skLineSegment(sketch, "E5.8.4.4", {"start": v(18.86, -3.13) * mm, "end": v(21.86, -4.86) * mm});
            skLineSegment(sketch, "E5.8.4.5", {"start": v(15.86, -4.86) * mm, "end": v(18.86, -3.13) * mm});
            skLineSegment(sketch, "E5.8.4.6", {"start": v(21.86, -4.86) * mm, "end": v(21.86, -8.33) * mm});
            skLineSegment(sketch, "E5.8.4.7", {"start": v(21.86, -8.33) * mm, "end": v(18.86, -10.06) * mm});
            skLineSegment(sketch, "E5.8.5.0", {"start": v(19.65, -1.85) * mm, "end": v(19.65, 1.62) * mm});
            skCircle(sketch, "E5.8.5.1", {"center": v(22.65, -0.12) * mm, "radius": 3 * mm, "construction": true});
            skPoint(sketch, "E5.8.5.2", {"position": v(24.15, -2.72) * mm});
            skLineSegment(sketch, "E5.8.5.3", {"start": v(22.65, -3.58) * mm, "end": v(19.65, -1.85) * mm});
            skLineSegment(sketch, "E5.8.5.4", {"start": v(22.65, 3.35) * mm, "end": v(25.65, 1.62) * mm});
            skLineSegment(sketch, "E5.8.5.5", {"start": v(19.65, 1.62) * mm, "end": v(22.65, 3.35) * mm});
            skLineSegment(sketch, "E5.8.5.6", {"start": v(25.65, 1.62) * mm, "end": v(25.65, -1.85) * mm});
            skLineSegment(sketch, "E5.8.5.7", {"start": v(25.65, -1.85) * mm, "end": v(22.65, -3.58) * mm});
            skLineSegment(sketch, "E5.8.6.0", {"start": v(23.43, 4.63) * mm, "end": v(23.43, 8.1) * mm});
            skCircle(sketch, "E5.8.6.1", {"center": v(26.43, 6.36) * mm, "radius": 3 * mm, "construction": true});
            skPoint(sketch, "E5.8.6.2", {"position": v(27.93, 3.76) * mm});
            skLineSegment(sketch, "E5.8.6.3", {"start": v(26.43, 2.9) * mm, "end": v(23.43, 4.63) * mm});
            skLineSegment(sketch, "E5.8.6.4", {"start": v(26.43, 9.82) * mm, "end": v(29.43, 8.1) * mm});
            skLineSegment(sketch, "E5.8.6.5", {"start": v(23.43, 8.1) * mm, "end": v(26.43, 9.82) * mm});
            skLineSegment(sketch, "E5.8.6.6", {"start": v(29.43, 8.1) * mm, "end": v(29.43, 4.63) * mm});
            skLineSegment(sketch, "E5.8.6.7", {"start": v(29.43, 4.63) * mm, "end": v(26.43, 2.9) * mm});
            skLineSegment(sketch, "E5.8.7.0", {"start": v(27.21, 11.1) * mm, "end": v(27.21, 14.57) * mm});
            skCircle(sketch, "E5.8.7.1", {"center": v(30.21, 12.84) * mm, "radius": 3 * mm, "construction": true});
            skPoint(sketch, "E5.8.7.2", {"position": v(31.71, 10.24) * mm});
            skLineSegment(sketch, "E5.8.7.3", {"start": v(30.21, 9.37) * mm, "end": v(27.21, 11.1) * mm});
            skLineSegment(sketch, "E5.8.7.4", {"start": v(30.21, 16.3) * mm, "end": v(33.21, 14.57) * mm});
            skLineSegment(sketch, "E5.8.7.5", {"start": v(27.21, 14.57) * mm, "end": v(30.21, 16.3) * mm});
            skLineSegment(sketch, "E5.8.7.6", {"start": v(33.21, 14.57) * mm, "end": v(33.21, 11.1) * mm});
            skLineSegment(sketch, "E5.8.7.7", {"start": v(33.21, 11.1) * mm, "end": v(30.21, 9.37) * mm});
            skLineSegment(sketch, "E5.8.8.0", {"start": v(31, 17.58) * mm, "end": v(31, 21.04) * mm});
            skCircle(sketch, "E5.8.8.1", {"center": v(34, 19.31) * mm, "radius": 3 * mm, "construction": true});
            skPoint(sketch, "E5.8.8.2", {"position": v(35.5, 16.71) * mm});
            skLineSegment(sketch, "E5.8.8.3", {"start": v(34, 15.85) * mm, "end": v(31, 17.58) * mm});
            skLineSegment(sketch, "E5.8.8.4", {"start": v(34, 22.78) * mm, "end": v(37, 21.04) * mm});
            skLineSegment(sketch, "E5.8.8.5", {"start": v(31, 21.04) * mm, "end": v(34, 22.78) * mm});
            skLineSegment(sketch, "E5.8.8.6", {"start": v(37, 21.04) * mm, "end": v(37, 17.58) * mm});
            skLineSegment(sketch, "E5.8.8.7", {"start": v(37, 17.58) * mm, "end": v(34, 15.85) * mm});
            skLineSegment(sketch, "E5.8.9.0", {"start": v(34.78, 24.06) * mm, "end": v(34.78, 27.52) * mm});
            skCircle(sketch, "E5.8.9.1", {"center": v(37.78, 25.79) * mm, "radius": 3 * mm, "construction": true});
            skPoint(sketch, "E5.8.9.2", {"position": v(39.28, 23.19) * mm});
            skLineSegment(sketch, "E5.8.9.3", {"start": v(37.78, 22.32) * mm, "end": v(34.78, 24.06) * mm});
            skLineSegment(sketch, "E5.8.9.4", {"start": v(37.78, 29.25) * mm, "end": v(40.78, 27.52) * mm});
            skLineSegment(sketch, "E5.8.9.5", {"start": v(34.78, 27.52) * mm, "end": v(37.78, 29.25) * mm});
            skLineSegment(sketch, "E5.8.9.6", {"start": v(40.78, 27.52) * mm, "end": v(40.78, 24.06) * mm});
            skLineSegment(sketch, "E5.8.9.7", {"start": v(40.78, 24.06) * mm, "end": v(37.78, 22.32) * mm});
            skLineSegment(sketch, "E5.9.0.0", {"start": v(8.23, -34.23) * mm, "end": v(8.23, -30.77) * mm});
            skCircle(sketch, "E5.9.0.1", {"center": v(11.23, -32.5) * mm, "radius": 3 * mm, "construction": true});
            skPoint(sketch, "E5.9.0.2", {"position": v(12.73, -35.1) * mm});
            skLineSegment(sketch, "E5.9.0.3", {"start": v(11.23, -35.96) * mm, "end": v(8.23, -34.23) * mm});
            skLineSegment(sketch, "E5.9.0.4", {"start": v(11.23, -29.03) * mm, "end": v(14.23, -30.77) * mm});
            skLineSegment(sketch, "E5.9.0.5", {"start": v(8.23, -30.77) * mm, "end": v(11.23, -29.03) * mm});
            skLineSegment(sketch, "E5.9.0.6", {"start": v(14.23, -30.77) * mm, "end": v(14.23, -34.23) * mm});
            skLineSegment(sketch, "E5.9.0.7", {"start": v(14.23, -34.23) * mm, "end": v(11.23, -35.96) * mm});
            skLineSegment(sketch, "E5.9.1.0", {"start": v(12.01, -27.75) * mm, "end": v(12.01, -24.29) * mm});
            skCircle(sketch, "E5.9.1.1", {"center": v(15.01, -26.02) * mm, "radius": 3 * mm, "construction": true});
            skPoint(sketch, "E5.9.1.2", {"position": v(16.51, -28.62) * mm});
            skLineSegment(sketch, "E5.9.1.3", {"start": v(15.01, -29.49) * mm, "end": v(12.01, -27.75) * mm});
            skLineSegment(sketch, "E5.9.1.4", {"start": v(15.01, -22.56) * mm, "end": v(18.01, -24.29) * mm});
            skLineSegment(sketch, "E5.9.1.5", {"start": v(12.01, -24.29) * mm, "end": v(15.01, -22.56) * mm});
            skLineSegment(sketch, "E5.9.1.6", {"start": v(18.01, -24.29) * mm, "end": v(18.01, -27.75) * mm});
            skLineSegment(sketch, "E5.9.1.7", {"start": v(18.01, -27.75) * mm, "end": v(15.01, -29.49) * mm});
            skLineSegment(sketch, "E5.9.2.0", {"start": v(15.8, -21.28) * mm, "end": v(15.8, -17.81) * mm});
            skCircle(sketch, "E5.9.2.1", {"center": v(18.8, -19.55) * mm, "radius": 3 * mm, "construction": true});
            skPoint(sketch, "E5.9.2.2", {"position": v(20.3, -22.14) * mm});
            skLineSegment(sketch, "E5.9.2.3", {"start": v(18.8, -23) * mm, "end": v(15.8, -21.28) * mm});
            skLineSegment(sketch, "E5.9.2.4", {"start": v(18.8, -16.08) * mm, "end": v(21.8, -17.81) * mm});
            skLineSegment(sketch, "E5.9.2.5", {"start": v(15.8, -17.81) * mm, "end": v(18.8, -16.08) * mm});
            skLineSegment(sketch, "E5.9.2.6", {"start": v(21.8, -17.81) * mm, "end": v(21.8, -21.28) * mm});
            skLineSegment(sketch, "E5.9.2.7", {"start": v(21.8, -21.28) * mm, "end": v(18.8, -23) * mm});
            skLineSegment(sketch, "E5.9.3.0", {"start": v(19.58, -14.8) * mm, "end": v(19.58, -11.34) * mm});
            skCircle(sketch, "E5.9.3.1", {"center": v(22.58, -13.07) * mm, "radius": 3 * mm, "construction": true});
            skPoint(sketch, "E5.9.3.2", {"position": v(24.08, -15.67) * mm});
            skLineSegment(sketch, "E5.9.3.3", {"start": v(22.58, -16.53) * mm, "end": v(19.58, -14.8) * mm});
            skLineSegment(sketch, "E5.9.3.4", {"start": v(22.58, -9.6) * mm, "end": v(25.58, -11.34) * mm});
            skLineSegment(sketch, "E5.9.3.5", {"start": v(19.58, -11.34) * mm, "end": v(22.58, -9.6) * mm});
            skLineSegment(sketch, "E5.9.3.6", {"start": v(25.58, -11.34) * mm, "end": v(25.58, -14.8) * mm});
            skLineSegment(sketch, "E5.9.3.7", {"start": v(25.58, -14.8) * mm, "end": v(22.58, -16.53) * mm});
            skLineSegment(sketch, "E5.9.4.0", {"start": v(23.36, -8.33) * mm, "end": v(23.36, -4.86) * mm});
            skCircle(sketch, "E5.9.4.1", {"center": v(26.36, -6.6) * mm, "radius": 3 * mm, "construction": true});
            skPoint(sketch, "E5.9.4.2", {"position": v(27.86, -9.2) * mm});
            skLineSegment(sketch, "E5.9.4.3", {"start": v(26.36, -10.06) * mm, "end": v(23.36, -8.33) * mm});
            skLineSegment(sketch, "E5.9.4.4", {"start": v(26.36, -3.13) * mm, "end": v(29.36, -4.86) * mm});
            skLineSegment(sketch, "E5.9.4.5", {"start": v(23.36, -4.86) * mm, "end": v(26.36, -3.13) * mm});
            skLineSegment(sketch, "E5.9.4.6", {"start": v(29.36, -4.86) * mm, "end": v(29.36, -8.33) * mm});
            skLineSegment(sketch, "E5.9.4.7", {"start": v(29.36, -8.33) * mm, "end": v(26.36, -10.06) * mm});
            skLineSegment(sketch, "E5.9.5.0", {"start": v(27.15, -1.85) * mm, "end": v(27.15, 1.62) * mm});
            skCircle(sketch, "E5.9.5.1", {"center": v(30.15, -0.12) * mm, "radius": 3 * mm, "construction": true});
            skPoint(sketch, "E5.9.5.2", {"position": v(31.65, -2.72) * mm});
            skLineSegment(sketch, "E5.9.5.3", {"start": v(30.15, -3.58) * mm, "end": v(27.15, -1.85) * mm});
            skLineSegment(sketch, "E5.9.5.4", {"start": v(30.15, 3.35) * mm, "end": v(33.15, 1.62) * mm});
            skLineSegment(sketch, "E5.9.5.5", {"start": v(27.15, 1.62) * mm, "end": v(30.15, 3.35) * mm});
            skLineSegment(sketch, "E5.9.5.6", {"start": v(33.15, 1.62) * mm, "end": v(33.15, -1.85) * mm});
            skLineSegment(sketch, "E5.9.5.7", {"start": v(33.15, -1.85) * mm, "end": v(30.15, -3.58) * mm});
            skLineSegment(sketch, "E5.9.6.0", {"start": v(30.93, 4.63) * mm, "end": v(30.93, 8.1) * mm});
            skCircle(sketch, "E5.9.6.1", {"center": v(33.93, 6.36) * mm, "radius": 3 * mm, "construction": true});
            skPoint(sketch, "E5.9.6.2", {"position": v(35.43, 3.76) * mm});
            skLineSegment(sketch, "E5.9.6.3", {"start": v(33.93, 2.9) * mm, "end": v(30.93, 4.63) * mm});
            skLineSegment(sketch, "E5.9.6.4", {"start": v(33.93, 9.82) * mm, "end": v(36.93, 8.1) * mm});
            skLineSegment(sketch, "E5.9.6.5", {"start": v(30.93, 8.1) * mm, "end": v(33.93, 9.82) * mm});
            skLineSegment(sketch, "E5.9.6.6", {"start": v(36.93, 8.1) * mm, "end": v(36.93, 4.63) * mm});
            skLineSegment(sketch, "E5.9.6.7", {"start": v(36.93, 4.63) * mm, "end": v(33.93, 2.9) * mm});
            skLineSegment(sketch, "E5.9.7.0", {"start": v(34.71, 11.1) * mm, "end": v(34.71, 14.57) * mm});
            skCircle(sketch, "E5.9.7.1", {"center": v(37.71, 12.84) * mm, "radius": 3 * mm, "construction": true});
            skPoint(sketch, "E5.9.7.2", {"position": v(39.21, 10.24) * mm});
            skLineSegment(sketch, "E5.9.7.3", {"start": v(37.71, 9.37) * mm, "end": v(34.71, 11.1) * mm});
            skLineSegment(sketch, "E5.9.7.4", {"start": v(37.71, 16.3) * mm, "end": v(40.71, 14.57) * mm});
            skLineSegment(sketch, "E5.9.7.5", {"start": v(34.71, 14.57) * mm, "end": v(37.71, 16.3) * mm});
            skLineSegment(sketch, "E5.9.7.6", {"start": v(40.71, 14.57) * mm, "end": v(40.71, 11.1) * mm});
            skLineSegment(sketch, "E5.9.7.7", {"start": v(40.71, 11.1) * mm, "end": v(37.71, 9.37) * mm});
            skLineSegment(sketch, "E5.9.8.0", {"start": v(38.5, 17.58) * mm, "end": v(38.5, 21.04) * mm});
            skCircle(sketch, "E5.9.8.1", {"center": v(41.5, 19.31) * mm, "radius": 3 * mm, "construction": true});
            skPoint(sketch, "E5.9.8.2", {"position": v(43, 16.71) * mm});
            skLineSegment(sketch, "E5.9.8.3", {"start": v(41.5, 15.85) * mm, "end": v(38.5, 17.58) * mm});
            skLineSegment(sketch, "E5.9.8.4", {"start": v(41.5, 22.78) * mm, "end": v(44.5, 21.04) * mm});
            skLineSegment(sketch, "E5.9.8.5", {"start": v(38.5, 21.04) * mm, "end": v(41.5, 22.78) * mm});
            skLineSegment(sketch, "E5.9.8.6", {"start": v(44.5, 21.04) * mm, "end": v(44.5, 17.58) * mm});
            skLineSegment(sketch, "E5.9.8.7", {"start": v(44.5, 17.58) * mm, "end": v(41.5, 15.85) * mm});
            skLineSegment(sketch, "E5.9.9.0", {"start": v(42.28, 24.06) * mm, "end": v(42.28, 27.52) * mm});
            skCircle(sketch, "E5.9.9.1", {"center": v(45.28, 25.79) * mm, "radius": 3 * mm, "construction": true});
            skPoint(sketch, "E5.9.9.2", {"position": v(46.78, 23.19) * mm});
            skLineSegment(sketch, "E5.9.9.3", {"start": v(45.28, 22.32) * mm, "end": v(42.28, 24.06) * mm});
            skLineSegment(sketch, "E5.9.9.4", {"start": v(45.28, 29.25) * mm, "end": v(48.28, 27.52) * mm});
            skLineSegment(sketch, "E5.9.9.5", {"start": v(42.28, 27.52) * mm, "end": v(45.28, 29.25) * mm});
            skLineSegment(sketch, "E5.9.9.6", {"start": v(48.28, 27.52) * mm, "end": v(48.28, 24.06) * mm});
            skLineSegment(sketch, "E5.9.9.7", {"start": v(48.28, 24.06) * mm, "end": v(45.28, 22.32) * mm});
            skLineSegment(sketch, "E5.direction1", {"start": v(-59.27, -34.23) * mm, "end": v(-51.77, -34.23) * mm, "construction": true});
            skLineSegment(sketch, "E5.direction2", {"start": v(-59.27, -34.23) * mm, "end": v(-55.49, -27.75) * mm, "construction": true});
            skLineSegment(sketch, "E6.0.0.10", {"start": v(-21.44, 30.53) * mm, "end": v(-21.44, 34) * mm});
            skCircle(sketch, "E6.3.0.10", {"center": v(-18.44, 32.26) * mm, "radius": 3 * mm, "construction": true});
            skPoint(sketch, "E6.5.0.10", {"position": v(-16.94, 29.67) * mm});
            skLineSegment(sketch, "E6.6.0.10", {"start": v(-18.44, 28.8) * mm, "end": v(-21.44, 30.53) * mm});
            skLineSegment(sketch, "E6.9.0.10", {"start": v(-18.44, 35.73) * mm, "end": v(-15.44, 34) * mm});
            skLineSegment(sketch, "E6.12.0.10", {"start": v(-21.44, 34) * mm, "end": v(-18.44, 35.73) * mm});
            skLineSegment(sketch, "E6.15.0.10", {"start": v(-15.44, 34) * mm, "end": v(-15.44, 30.53) * mm});
            skLineSegment(sketch, "E6.18.0.10", {"start": v(-15.44, 30.53) * mm, "end": v(-18.44, 28.8) * mm});
            skLineSegment(sketch, "E6.0.0.11", {"start": v(-17.66, 37) * mm, "end": v(-17.66, 40.47) * mm});
            skCircle(sketch, "E6.3.0.11", {"center": v(-14.66, 38.74) * mm, "radius": 3 * mm, "construction": true});
            skPoint(sketch, "E6.5.0.11", {"position": v(-13.16, 36.14) * mm});
            skLineSegment(sketch, "E6.6.0.11", {"start": v(-14.66, 35.28) * mm, "end": v(-17.66, 37) * mm});
            skLineSegment(sketch, "E6.9.0.11", {"start": v(-14.66, 42.2) * mm, "end": v(-11.66, 40.47) * mm});
            skLineSegment(sketch, "E6.12.0.11", {"start": v(-17.66, 40.47) * mm, "end": v(-14.66, 42.2) * mm});
            skLineSegment(sketch, "E6.15.0.11", {"start": v(-11.66, 40.47) * mm, "end": v(-11.66, 37) * mm});
            skLineSegment(sketch, "E6.18.0.11", {"start": v(-11.66, 37) * mm, "end": v(-14.66, 35.28) * mm});
            skLineSegment(sketch, "E6.0.1.10", {"start": v(-13.94, 30.53) * mm, "end": v(-13.94, 34) * mm});
            skCircle(sketch, "E6.3.1.10", {"center": v(-10.94, 32.26) * mm, "radius": 3 * mm, "construction": true});
            skPoint(sketch, "E6.5.1.10", {"position": v(-9.44, 29.67) * mm});
            skLineSegment(sketch, "E6.6.1.10", {"start": v(-10.94, 28.8) * mm, "end": v(-13.94, 30.53) * mm});
            skLineSegment(sketch, "E6.9.1.10", {"start": v(-10.94, 35.73) * mm, "end": v(-7.94, 34) * mm});
            skLineSegment(sketch, "E6.12.1.10", {"start": v(-13.94, 34) * mm, "end": v(-10.94, 35.73) * mm});
            skLineSegment(sketch, "E6.15.1.10", {"start": v(-7.94, 34) * mm, "end": v(-7.94, 30.53) * mm});
            skLineSegment(sketch, "E6.18.1.10", {"start": v(-7.94, 30.53) * mm, "end": v(-10.94, 28.8) * mm});
            skLineSegment(sketch, "E6.0.1.11", {"start": v(-10.16, 37) * mm, "end": v(-10.16, 40.47) * mm});
            skCircle(sketch, "E6.3.1.11", {"center": v(-7.16, 38.74) * mm, "radius": 3 * mm, "construction": true});
            skPoint(sketch, "E6.5.1.11", {"position": v(-5.66, 36.14) * mm});
            skLineSegment(sketch, "E6.6.1.11", {"start": v(-7.16, 35.28) * mm, "end": v(-10.16, 37) * mm});
            skLineSegment(sketch, "E6.9.1.11", {"start": v(-7.16, 42.2) * mm, "end": v(-4.16, 40.47) * mm});
            skLineSegment(sketch, "E6.12.1.11", {"start": v(-10.16, 40.47) * mm, "end": v(-7.16, 42.2) * mm});
            skLineSegment(sketch, "E6.15.1.11", {"start": v(-4.16, 40.47) * mm, "end": v(-4.16, 37) * mm});
            skLineSegment(sketch, "E6.18.1.11", {"start": v(-4.16, 37) * mm, "end": v(-7.16, 35.28) * mm});
            skLineSegment(sketch, "E6.0.2.10", {"start": v(-6.44, 30.53) * mm, "end": v(-6.44, 34) * mm});
            skCircle(sketch, "E6.3.2.10", {"center": v(-3.44, 32.26) * mm, "radius": 3 * mm, "construction": true});
            skPoint(sketch, "E6.5.2.10", {"position": v(-1.94, 29.67) * mm});
            skLineSegment(sketch, "E6.6.2.10", {"start": v(-3.44, 28.8) * mm, "end": v(-6.44, 30.53) * mm});
            skLineSegment(sketch, "E6.9.2.10", {"start": v(-3.44, 35.73) * mm, "end": v(-0.44, 34) * mm});
            skLineSegment(sketch, "E6.12.2.10", {"start": v(-6.44, 34) * mm, "end": v(-3.44, 35.73) * mm});
            skLineSegment(sketch, "E6.15.2.10", {"start": v(-0.44, 34) * mm, "end": v(-0.44, 30.53) * mm});
            skLineSegment(sketch, "E6.18.2.10", {"start": v(-0.44, 30.53) * mm, "end": v(-3.44, 28.8) * mm});
            skLineSegment(sketch, "E6.0.2.11", {"start": v(-2.66, 37) * mm, "end": v(-2.66, 40.47) * mm});
            skCircle(sketch, "E6.3.2.11", {"center": v(0.34, 38.74) * mm, "radius": 3 * mm, "construction": true});
            skPoint(sketch, "E6.5.2.11", {"position": v(1.84, 36.14) * mm});
            skLineSegment(sketch, "E6.6.2.11", {"start": v(0.34, 35.28) * mm, "end": v(-2.66, 37) * mm});
            skLineSegment(sketch, "E6.9.2.11", {"start": v(0.34, 42.2) * mm, "end": v(3.34, 40.47) * mm});
            skLineSegment(sketch, "E6.12.2.11", {"start": v(-2.66, 40.47) * mm, "end": v(0.34, 42.2) * mm});
            skLineSegment(sketch, "E6.15.2.11", {"start": v(3.34, 40.47) * mm, "end": v(3.34, 37) * mm});
            skLineSegment(sketch, "E6.18.2.11", {"start": v(3.34, 37) * mm, "end": v(0.34, 35.28) * mm});
            skLineSegment(sketch, "E6.0.3.10", {"start": v(1.06, 30.53) * mm, "end": v(1.06, 34) * mm});
            skCircle(sketch, "E6.3.3.10", {"center": v(4.06, 32.26) * mm, "radius": 3 * mm, "construction": true});
            skPoint(sketch, "E6.5.3.10", {"position": v(5.56, 29.67) * mm});
            skLineSegment(sketch, "E6.6.3.10", {"start": v(4.06, 28.8) * mm, "end": v(1.06, 30.53) * mm});
            skLineSegment(sketch, "E6.9.3.10", {"start": v(4.06, 35.73) * mm, "end": v(7.06, 34) * mm});
            skLineSegment(sketch, "E6.12.3.10", {"start": v(1.06, 34) * mm, "end": v(4.06, 35.73) * mm});
            skLineSegment(sketch, "E6.15.3.10", {"start": v(7.06, 34) * mm, "end": v(7.06, 30.53) * mm});
            skLineSegment(sketch, "E6.18.3.10", {"start": v(7.06, 30.53) * mm, "end": v(4.06, 28.8) * mm});
            skLineSegment(sketch, "E6.0.3.11", {"start": v(4.84, 37) * mm, "end": v(4.84, 40.47) * mm});
            skCircle(sketch, "E6.3.3.11", {"center": v(7.84, 38.74) * mm, "radius": 3 * mm, "construction": true});
            skPoint(sketch, "E6.5.3.11", {"position": v(9.34, 36.14) * mm});
            skLineSegment(sketch, "E6.6.3.11", {"start": v(7.84, 35.28) * mm, "end": v(4.84, 37) * mm});
            skLineSegment(sketch, "E6.9.3.11", {"start": v(7.84, 42.2) * mm, "end": v(10.84, 40.47) * mm});
            skLineSegment(sketch, "E6.12.3.11", {"start": v(4.84, 40.47) * mm, "end": v(7.84, 42.2) * mm});
            skLineSegment(sketch, "E6.15.3.11", {"start": v(10.84, 40.47) * mm, "end": v(10.84, 37) * mm});
            skLineSegment(sketch, "E6.18.3.11", {"start": v(10.84, 37) * mm, "end": v(7.84, 35.28) * mm});
            skLineSegment(sketch, "E6.0.4.10", {"start": v(8.56, 30.53) * mm, "end": v(8.56, 34) * mm});
            skCircle(sketch, "E6.3.4.10", {"center": v(11.56, 32.26) * mm, "radius": 3 * mm, "construction": true});
            skPoint(sketch, "E6.5.4.10", {"position": v(13.06, 29.67) * mm});
            skLineSegment(sketch, "E6.6.4.10", {"start": v(11.56, 28.8) * mm, "end": v(8.56, 30.53) * mm});
            skLineSegment(sketch, "E6.9.4.10", {"start": v(11.56, 35.73) * mm, "end": v(14.56, 34) * mm});
            skLineSegment(sketch, "E6.12.4.10", {"start": v(8.56, 34) * mm, "end": v(11.56, 35.73) * mm});
            skLineSegment(sketch, "E6.15.4.10", {"start": v(14.56, 34) * mm, "end": v(14.56, 30.53) * mm});
            skLineSegment(sketch, "E6.18.4.10", {"start": v(14.56, 30.53) * mm, "end": v(11.56, 28.8) * mm});
            skLineSegment(sketch, "E6.0.4.11", {"start": v(12.34, 37) * mm, "end": v(12.34, 40.47) * mm});
            skCircle(sketch, "E6.3.4.11", {"center": v(15.34, 38.74) * mm, "radius": 3 * mm, "construction": true});
            skPoint(sketch, "E6.5.4.11", {"position": v(16.84, 36.14) * mm});
            skLineSegment(sketch, "E6.6.4.11", {"start": v(15.34, 35.28) * mm, "end": v(12.34, 37) * mm});
            skLineSegment(sketch, "E6.9.4.11", {"start": v(15.34, 42.2) * mm, "end": v(18.34, 40.47) * mm});
            skLineSegment(sketch, "E6.12.4.11", {"start": v(12.34, 40.47) * mm, "end": v(15.34, 42.2) * mm});
            skLineSegment(sketch, "E6.15.4.11", {"start": v(18.34, 40.47) * mm, "end": v(18.34, 37) * mm});
            skLineSegment(sketch, "E6.18.4.11", {"start": v(18.34, 37) * mm, "end": v(15.34, 35.28) * mm});
            skLineSegment(sketch, "E6.0.5.10", {"start": v(16.06, 30.53) * mm, "end": v(16.06, 34) * mm});
            skCircle(sketch, "E6.3.5.10", {"center": v(19.06, 32.26) * mm, "radius": 3 * mm, "construction": true});
            skPoint(sketch, "E6.5.5.10", {"position": v(20.56, 29.67) * mm});
            skLineSegment(sketch, "E6.6.5.10", {"start": v(19.06, 28.8) * mm, "end": v(16.06, 30.53) * mm});
            skLineSegment(sketch, "E6.9.5.10", {"start": v(19.06, 35.73) * mm, "end": v(22.06, 34) * mm});
            skLineSegment(sketch, "E6.12.5.10", {"start": v(16.06, 34) * mm, "end": v(19.06, 35.73) * mm});
            skLineSegment(sketch, "E6.15.5.10", {"start": v(22.06, 34) * mm, "end": v(22.06, 30.53) * mm});
            skLineSegment(sketch, "E6.18.5.10", {"start": v(22.06, 30.53) * mm, "end": v(19.06, 28.8) * mm});
            skLineSegment(sketch, "E6.0.5.11", {"start": v(19.84, 37) * mm, "end": v(19.84, 40.47) * mm});
            skCircle(sketch, "E6.3.5.11", {"center": v(22.84, 38.74) * mm, "radius": 3 * mm, "construction": true});
            skPoint(sketch, "E6.5.5.11", {"position": v(24.34, 36.14) * mm});
            skLineSegment(sketch, "E6.6.5.11", {"start": v(22.84, 35.28) * mm, "end": v(19.84, 37) * mm});
            skLineSegment(sketch, "E6.9.5.11", {"start": v(22.84, 42.2) * mm, "end": v(25.84, 40.47) * mm});
            skLineSegment(sketch, "E6.12.5.11", {"start": v(19.84, 40.47) * mm, "end": v(22.84, 42.2) * mm});
            skLineSegment(sketch, "E6.15.5.11", {"start": v(25.84, 40.47) * mm, "end": v(25.84, 37) * mm});
            skLineSegment(sketch, "E6.18.5.11", {"start": v(25.84, 37) * mm, "end": v(22.84, 35.28) * mm});
            skLineSegment(sketch, "E6.0.6.10", {"start": v(23.56, 30.53) * mm, "end": v(23.56, 34) * mm});
            skCircle(sketch, "E6.3.6.10", {"center": v(26.56, 32.26) * mm, "radius": 3 * mm, "construction": true});
            skPoint(sketch, "E6.5.6.10", {"position": v(28.06, 29.67) * mm});
            skLineSegment(sketch, "E6.6.6.10", {"start": v(26.56, 28.8) * mm, "end": v(23.56, 30.53) * mm});
            skLineSegment(sketch, "E6.9.6.10", {"start": v(26.56, 35.73) * mm, "end": v(29.56, 34) * mm});
            skLineSegment(sketch, "E6.12.6.10", {"start": v(23.56, 34) * mm, "end": v(26.56, 35.73) * mm});
            skLineSegment(sketch, "E6.15.6.10", {"start": v(29.56, 34) * mm, "end": v(29.56, 30.53) * mm});
            skLineSegment(sketch, "E6.18.6.10", {"start": v(29.56, 30.53) * mm, "end": v(26.56, 28.8) * mm});
            skLineSegment(sketch, "E6.0.6.11", {"start": v(27.34, 37) * mm, "end": v(27.34, 40.47) * mm});
            skCircle(sketch, "E6.3.6.11", {"center": v(30.34, 38.74) * mm, "radius": 3 * mm, "construction": true});
            skPoint(sketch, "E6.5.6.11", {"position": v(31.84, 36.14) * mm});
            skLineSegment(sketch, "E6.6.6.11", {"start": v(30.34, 35.28) * mm, "end": v(27.34, 37) * mm});
            skLineSegment(sketch, "E6.9.6.11", {"start": v(30.34, 42.2) * mm, "end": v(33.34, 40.47) * mm});
            skLineSegment(sketch, "E6.12.6.11", {"start": v(27.34, 40.47) * mm, "end": v(30.34, 42.2) * mm});
            skLineSegment(sketch, "E6.15.6.11", {"start": v(33.34, 40.47) * mm, "end": v(33.34, 37) * mm});
            skLineSegment(sketch, "E6.18.6.11", {"start": v(33.34, 37) * mm, "end": v(30.34, 35.28) * mm});
            skLineSegment(sketch, "E6.0.7.10", {"start": v(31.06, 30.53) * mm, "end": v(31.06, 34) * mm});
            skCircle(sketch, "E6.3.7.10", {"center": v(34.06, 32.26) * mm, "radius": 3 * mm, "construction": true});
            skPoint(sketch, "E6.5.7.10", {"position": v(35.56, 29.67) * mm});
            skLineSegment(sketch, "E6.6.7.10", {"start": v(34.06, 28.8) * mm, "end": v(31.06, 30.53) * mm});
            skLineSegment(sketch, "E6.9.7.10", {"start": v(34.06, 35.73) * mm, "end": v(37.06, 34) * mm});
            skLineSegment(sketch, "E6.12.7.10", {"start": v(31.06, 34) * mm, "end": v(34.06, 35.73) * mm});
            skLineSegment(sketch, "E6.15.7.10", {"start": v(37.06, 34) * mm, "end": v(37.06, 30.53) * mm});
            skLineSegment(sketch, "E6.18.7.10", {"start": v(37.06, 30.53) * mm, "end": v(34.06, 28.8) * mm});
            skLineSegment(sketch, "E6.0.7.11", {"start": v(34.84, 37) * mm, "end": v(34.84, 40.47) * mm});
            skCircle(sketch, "E6.3.7.11", {"center": v(37.84, 38.74) * mm, "radius": 3 * mm, "construction": true});
            skPoint(sketch, "E6.5.7.11", {"position": v(39.34, 36.14) * mm});
            skLineSegment(sketch, "E6.6.7.11", {"start": v(37.84, 35.28) * mm, "end": v(34.84, 37) * mm});
            skLineSegment(sketch, "E6.9.7.11", {"start": v(37.84, 42.2) * mm, "end": v(40.84, 40.47) * mm});
            skLineSegment(sketch, "E6.12.7.11", {"start": v(34.84, 40.47) * mm, "end": v(37.84, 42.2) * mm});
            skLineSegment(sketch, "E6.15.7.11", {"start": v(40.84, 40.47) * mm, "end": v(40.84, 37) * mm});
            skLineSegment(sketch, "E6.18.7.11", {"start": v(40.84, 37) * mm, "end": v(37.84, 35.28) * mm});
            skLineSegment(sketch, "E6.0.8.10", {"start": v(38.56, 30.53) * mm, "end": v(38.56, 34) * mm});
            skCircle(sketch, "E6.3.8.10", {"center": v(41.56, 32.26) * mm, "radius": 3 * mm, "construction": true});
            skPoint(sketch, "E6.5.8.10", {"position": v(43.06, 29.67) * mm});
            skLineSegment(sketch, "E6.6.8.10", {"start": v(41.56, 28.8) * mm, "end": v(38.56, 30.53) * mm});
            skLineSegment(sketch, "E6.9.8.10", {"start": v(41.56, 35.73) * mm, "end": v(44.56, 34) * mm});
            skLineSegment(sketch, "E6.12.8.10", {"start": v(38.56, 34) * mm, "end": v(41.56, 35.73) * mm});
            skLineSegment(sketch, "E6.15.8.10", {"start": v(44.56, 34) * mm, "end": v(44.56, 30.53) * mm});
            skLineSegment(sketch, "E6.18.8.10", {"start": v(44.56, 30.53) * mm, "end": v(41.56, 28.8) * mm});
            skLineSegment(sketch, "E6.0.8.11", {"start": v(42.34, 37) * mm, "end": v(42.34, 40.47) * mm});
            skCircle(sketch, "E6.3.8.11", {"center": v(45.34, 38.74) * mm, "radius": 3 * mm, "construction": true});
            skPoint(sketch, "E6.5.8.11", {"position": v(46.84, 36.14) * mm});
            skLineSegment(sketch, "E6.6.8.11", {"start": v(45.34, 35.28) * mm, "end": v(42.34, 37) * mm});
            skLineSegment(sketch, "E6.9.8.11", {"start": v(45.34, 42.2) * mm, "end": v(48.34, 40.47) * mm});
            skLineSegment(sketch, "E6.12.8.11", {"start": v(42.34, 40.47) * mm, "end": v(45.34, 42.2) * mm});
            skLineSegment(sketch, "E6.15.8.11", {"start": v(48.34, 40.47) * mm, "end": v(48.34, 37) * mm});
            skLineSegment(sketch, "E6.18.8.11", {"start": v(48.34, 37) * mm, "end": v(45.34, 35.28) * mm});
            skLineSegment(sketch, "E6.0.9.10", {"start": v(46.06, 30.53) * mm, "end": v(46.06, 34) * mm});
            skCircle(sketch, "E6.3.9.10", {"center": v(49.06, 32.26) * mm, "radius": 3 * mm, "construction": true});
            skPoint(sketch, "E6.5.9.10", {"position": v(50.56, 29.67) * mm});
            skLineSegment(sketch, "E6.6.9.10", {"start": v(49.06, 28.8) * mm, "end": v(46.06, 30.53) * mm});
            skLineSegment(sketch, "E6.9.9.10", {"start": v(49.06, 35.73) * mm, "end": v(52.06, 34) * mm});
            skLineSegment(sketch, "E6.12.9.10", {"start": v(46.06, 34) * mm, "end": v(49.06, 35.73) * mm});
            skLineSegment(sketch, "E6.15.9.10", {"start": v(52.06, 34) * mm, "end": v(52.06, 30.53) * mm});
            skLineSegment(sketch, "E6.18.9.10", {"start": v(52.06, 30.53) * mm, "end": v(49.06, 28.8) * mm});
            skLineSegment(sketch, "E6.0.9.11", {"start": v(49.84, 37) * mm, "end": v(49.84, 40.47) * mm});
            skCircle(sketch, "E6.3.9.11", {"center": v(52.84, 38.74) * mm, "radius": 3 * mm, "construction": true});
            skPoint(sketch, "E6.5.9.11", {"position": v(54.34, 36.14) * mm});
            skLineSegment(sketch, "E6.6.9.11", {"start": v(52.84, 35.28) * mm, "end": v(49.84, 37) * mm});
            skLineSegment(sketch, "E6.9.9.11", {"start": v(52.84, 42.2) * mm, "end": v(55.84, 40.47) * mm});
            skLineSegment(sketch, "E6.12.9.11", {"start": v(49.84, 40.47) * mm, "end": v(52.84, 42.2) * mm});
            skLineSegment(sketch, "E6.15.9.11", {"start": v(55.84, 40.47) * mm, "end": v(55.84, 37) * mm});
            skLineSegment(sketch, "E6.18.9.11", {"start": v(55.84, 37) * mm, "end": v(52.84, 35.28) * mm});
            skLineSegment(sketch, "E7.0.10.0", {"start": v(15.73, -34.23) * mm, "end": v(15.73, -30.77) * mm});
            skCircle(sketch, "E7.3.10.0", {"center": v(18.73, -32.5) * mm, "radius": 3 * mm, "construction": true});
            skPoint(sketch, "E7.5.10.0", {"position": v(20.23, -35.1) * mm});
            skLineSegment(sketch, "E7.6.10.0", {"start": v(18.73, -35.96) * mm, "end": v(15.73, -34.23) * mm});
            skLineSegment(sketch, "E7.9.10.0", {"start": v(18.73, -29.03) * mm, "end": v(21.73, -30.77) * mm});
            skLineSegment(sketch, "E7.12.10.0", {"start": v(15.73, -30.77) * mm, "end": v(18.73, -29.03) * mm});
            skLineSegment(sketch, "E7.15.10.0", {"start": v(21.73, -30.77) * mm, "end": v(21.73, -34.23) * mm});
            skLineSegment(sketch, "E7.18.10.0", {"start": v(21.73, -34.23) * mm, "end": v(18.73, -35.96) * mm});
            skLineSegment(sketch, "E7.0.10.1", {"start": v(19.51, -27.75) * mm, "end": v(19.51, -24.29) * mm});
            skCircle(sketch, "E7.3.10.1", {"center": v(22.51, -26.02) * mm, "radius": 3 * mm, "construction": true});
            skPoint(sketch, "E7.5.10.1", {"position": v(24.01, -28.62) * mm});
            skLineSegment(sketch, "E7.6.10.1", {"start": v(22.51, -29.49) * mm, "end": v(19.51, -27.75) * mm});
            skLineSegment(sketch, "E7.9.10.1", {"start": v(22.51, -22.56) * mm, "end": v(25.51, -24.29) * mm});
            skLineSegment(sketch, "E7.12.10.1", {"start": v(19.51, -24.29) * mm, "end": v(22.51, -22.56) * mm});
            skLineSegment(sketch, "E7.15.10.1", {"start": v(25.51, -24.29) * mm, "end": v(25.51, -27.75) * mm});
            skLineSegment(sketch, "E7.18.10.1", {"start": v(25.51, -27.75) * mm, "end": v(22.51, -29.49) * mm});
            skLineSegment(sketch, "E7.0.10.2", {"start": v(23.3, -21.28) * mm, "end": v(23.3, -17.81) * mm});
            skCircle(sketch, "E7.3.10.2", {"center": v(26.3, -19.55) * mm, "radius": 3 * mm, "construction": true});
            skPoint(sketch, "E7.5.10.2", {"position": v(27.8, -22.14) * mm});
            skLineSegment(sketch, "E7.6.10.2", {"start": v(26.3, -23) * mm, "end": v(23.3, -21.28) * mm});
            skLineSegment(sketch, "E7.9.10.2", {"start": v(26.3, -16.08) * mm, "end": v(29.3, -17.81) * mm});
            skLineSegment(sketch, "E7.12.10.2", {"start": v(23.3, -17.81) * mm, "end": v(26.3, -16.08) * mm});
            skLineSegment(sketch, "E7.15.10.2", {"start": v(29.3, -17.81) * mm, "end": v(29.3, -21.28) * mm});
            skLineSegment(sketch, "E7.18.10.2", {"start": v(29.3, -21.28) * mm, "end": v(26.3, -23) * mm});
            skLineSegment(sketch, "E7.0.10.3", {"start": v(27.08, -14.8) * mm, "end": v(27.08, -11.34) * mm});
            skCircle(sketch, "E7.3.10.3", {"center": v(30.08, -13.07) * mm, "radius": 3 * mm, "construction": true});
            skPoint(sketch, "E7.5.10.3", {"position": v(31.58, -15.67) * mm});
            skLineSegment(sketch, "E7.6.10.3", {"start": v(30.08, -16.53) * mm, "end": v(27.08, -14.8) * mm});
            skLineSegment(sketch, "E7.9.10.3", {"start": v(30.08, -9.6) * mm, "end": v(33.08, -11.34) * mm});
            skLineSegment(sketch, "E7.12.10.3", {"start": v(27.08, -11.34) * mm, "end": v(30.08, -9.6) * mm});
            skLineSegment(sketch, "E7.15.10.3", {"start": v(33.08, -11.34) * mm, "end": v(33.08, -14.8) * mm});
            skLineSegment(sketch, "E7.18.10.3", {"start": v(33.08, -14.8) * mm, "end": v(30.08, -16.53) * mm});
            skLineSegment(sketch, "E7.0.10.4", {"start": v(30.86, -8.33) * mm, "end": v(30.86, -4.86) * mm});
            skCircle(sketch, "E7.3.10.4", {"center": v(33.86, -6.6) * mm, "radius": 3 * mm, "construction": true});
            skPoint(sketch, "E7.5.10.4", {"position": v(35.36, -9.2) * mm});
            skLineSegment(sketch, "E7.6.10.4", {"start": v(33.86, -10.06) * mm, "end": v(30.86, -8.33) * mm});
            skLineSegment(sketch, "E7.9.10.4", {"start": v(33.86, -3.13) * mm, "end": v(36.86, -4.86) * mm});
            skLineSegment(sketch, "E7.12.10.4", {"start": v(30.86, -4.86) * mm, "end": v(33.86, -3.13) * mm});
            skLineSegment(sketch, "E7.15.10.4", {"start": v(36.86, -4.86) * mm, "end": v(36.86, -8.33) * mm});
            skLineSegment(sketch, "E7.18.10.4", {"start": v(36.86, -8.33) * mm, "end": v(33.86, -10.06) * mm});
            skLineSegment(sketch, "E7.0.10.5", {"start": v(34.65, -1.85) * mm, "end": v(34.65, 1.62) * mm});
            skCircle(sketch, "E7.3.10.5", {"center": v(37.65, -0.12) * mm, "radius": 3 * mm, "construction": true});
            skPoint(sketch, "E7.5.10.5", {"position": v(39.15, -2.72) * mm});
            skLineSegment(sketch, "E7.6.10.5", {"start": v(37.65, -3.58) * mm, "end": v(34.65, -1.85) * mm});
            skLineSegment(sketch, "E7.9.10.5", {"start": v(37.65, 3.35) * mm, "end": v(40.65, 1.62) * mm});
            skLineSegment(sketch, "E7.12.10.5", {"start": v(34.65, 1.62) * mm, "end": v(37.65, 3.35) * mm});
            skLineSegment(sketch, "E7.15.10.5", {"start": v(40.65, 1.62) * mm, "end": v(40.65, -1.85) * mm});
            skLineSegment(sketch, "E7.18.10.5", {"start": v(40.65, -1.85) * mm, "end": v(37.65, -3.58) * mm});
            skLineSegment(sketch, "E7.0.10.6", {"start": v(38.43, 4.63) * mm, "end": v(38.43, 8.1) * mm});
            skCircle(sketch, "E7.3.10.6", {"center": v(41.43, 6.36) * mm, "radius": 3 * mm, "construction": true});
            skPoint(sketch, "E7.5.10.6", {"position": v(42.93, 3.76) * mm});
            skLineSegment(sketch, "E7.6.10.6", {"start": v(41.43, 2.9) * mm, "end": v(38.43, 4.63) * mm});
            skLineSegment(sketch, "E7.9.10.6", {"start": v(41.43, 9.82) * mm, "end": v(44.43, 8.1) * mm});
            skLineSegment(sketch, "E7.12.10.6", {"start": v(38.43, 8.1) * mm, "end": v(41.43, 9.82) * mm});
            skLineSegment(sketch, "E7.15.10.6", {"start": v(44.43, 8.1) * mm, "end": v(44.43, 4.63) * mm});
            skLineSegment(sketch, "E7.18.10.6", {"start": v(44.43, 4.63) * mm, "end": v(41.43, 2.9) * mm});
            skLineSegment(sketch, "E7.0.10.7", {"start": v(42.21, 11.1) * mm, "end": v(42.21, 14.57) * mm});
            skCircle(sketch, "E7.3.10.7", {"center": v(45.21, 12.84) * mm, "radius": 3 * mm, "construction": true});
            skPoint(sketch, "E7.5.10.7", {"position": v(46.71, 10.24) * mm});
            skLineSegment(sketch, "E7.6.10.7", {"start": v(45.21, 9.37) * mm, "end": v(42.21, 11.1) * mm});
            skLineSegment(sketch, "E7.9.10.7", {"start": v(45.21, 16.3) * mm, "end": v(48.21, 14.57) * mm});
            skLineSegment(sketch, "E7.12.10.7", {"start": v(42.21, 14.57) * mm, "end": v(45.21, 16.3) * mm});
            skLineSegment(sketch, "E7.15.10.7", {"start": v(48.21, 14.57) * mm, "end": v(48.21, 11.1) * mm});
            skLineSegment(sketch, "E7.18.10.7", {"start": v(48.21, 11.1) * mm, "end": v(45.21, 9.37) * mm});
            skLineSegment(sketch, "E7.0.10.8", {"start": v(46, 17.58) * mm, "end": v(46, 21.04) * mm});
            skCircle(sketch, "E7.3.10.8", {"center": v(49, 19.31) * mm, "radius": 3 * mm, "construction": true});
            skPoint(sketch, "E7.5.10.8", {"position": v(50.5, 16.71) * mm});
            skLineSegment(sketch, "E7.6.10.8", {"start": v(49, 15.85) * mm, "end": v(46, 17.58) * mm});
            skLineSegment(sketch, "E7.9.10.8", {"start": v(49, 22.78) * mm, "end": v(52, 21.04) * mm});
            skLineSegment(sketch, "E7.12.10.8", {"start": v(46, 21.04) * mm, "end": v(49, 22.78) * mm});
            skLineSegment(sketch, "E7.15.10.8", {"start": v(52, 21.04) * mm, "end": v(52, 17.58) * mm});
            skLineSegment(sketch, "E7.18.10.8", {"start": v(52, 17.58) * mm, "end": v(49, 15.85) * mm});
            skLineSegment(sketch, "E7.0.10.9", {"start": v(49.78, 24.06) * mm, "end": v(49.78, 27.52) * mm});
            skCircle(sketch, "E7.3.10.9", {"center": v(52.78, 25.79) * mm, "radius": 3 * mm, "construction": true});
            skPoint(sketch, "E7.5.10.9", {"position": v(54.28, 23.19) * mm});
            skLineSegment(sketch, "E7.6.10.9", {"start": v(52.78, 22.32) * mm, "end": v(49.78, 24.06) * mm});
            skLineSegment(sketch, "E7.9.10.9", {"start": v(52.78, 29.25) * mm, "end": v(55.78, 27.52) * mm});
            skLineSegment(sketch, "E7.12.10.9", {"start": v(49.78, 27.52) * mm, "end": v(52.78, 29.25) * mm});
            skLineSegment(sketch, "E7.15.10.9", {"start": v(55.78, 27.52) * mm, "end": v(55.78, 24.06) * mm});
            skLineSegment(sketch, "E7.18.10.9", {"start": v(55.78, 24.06) * mm, "end": v(52.78, 22.32) * mm});
            skLineSegment(sketch, "E7.0.10.10", {"start": v(53.56, 30.53) * mm, "end": v(53.56, 34) * mm});
            skCircle(sketch, "E7.3.10.10", {"center": v(56.56, 32.26) * mm, "radius": 3 * mm, "construction": true});
            skPoint(sketch, "E7.5.10.10", {"position": v(58.06, 29.67) * mm});
            skLineSegment(sketch, "E7.6.10.10", {"start": v(56.56, 28.8) * mm, "end": v(53.56, 30.53) * mm});
            skLineSegment(sketch, "E7.9.10.10", {"start": v(56.56, 35.73) * mm, "end": v(59.56, 34) * mm});
            skLineSegment(sketch, "E7.12.10.10", {"start": v(53.56, 34) * mm, "end": v(56.56, 35.73) * mm});
            skLineSegment(sketch, "E7.15.10.10", {"start": v(59.56, 34) * mm, "end": v(59.56, 30.53) * mm});
            skLineSegment(sketch, "E7.18.10.10", {"start": v(59.56, 30.53) * mm, "end": v(56.56, 28.8) * mm});
            skLineSegment(sketch, "E7.0.10.11", {"start": v(57.34, 37) * mm, "end": v(57.34, 40.47) * mm});
            skCircle(sketch, "E7.3.10.11", {"center": v(60.34, 38.74) * mm, "radius": 3 * mm, "construction": true});
            skPoint(sketch, "E7.5.10.11", {"position": v(61.84, 36.14) * mm});
            skLineSegment(sketch, "E7.6.10.11", {"start": v(60.34, 35.28) * mm, "end": v(57.34, 37) * mm});
            skLineSegment(sketch, "E7.9.10.11", {"start": v(60.34, 42.2) * mm, "end": v(63.34, 40.47) * mm});
            skLineSegment(sketch, "E7.12.10.11", {"start": v(57.34, 40.47) * mm, "end": v(60.34, 42.2) * mm});
            skLineSegment(sketch, "E7.15.10.11", {"start": v(63.34, 40.47) * mm, "end": v(63.34, 37) * mm});
            skLineSegment(sketch, "E7.18.10.11", {"start": v(63.34, 37) * mm, "end": v(60.34, 35.28) * mm});
            skLineSegment(sketch, "E7.0.11.0", {"start": v(23.23, -34.23) * mm, "end": v(23.23, -30.77) * mm});
            skCircle(sketch, "E7.3.11.0", {"center": v(26.23, -32.5) * mm, "radius": 3 * mm, "construction": true});
            skPoint(sketch, "E7.5.11.0", {"position": v(27.73, -35.1) * mm});
            skLineSegment(sketch, "E7.6.11.0", {"start": v(26.23, -35.96) * mm, "end": v(23.23, -34.23) * mm});
            skLineSegment(sketch, "E7.9.11.0", {"start": v(26.23, -29.03) * mm, "end": v(29.23, -30.77) * mm});
            skLineSegment(sketch, "E7.12.11.0", {"start": v(23.23, -30.77) * mm, "end": v(26.23, -29.03) * mm});
            skLineSegment(sketch, "E7.15.11.0", {"start": v(29.23, -30.77) * mm, "end": v(29.23, -34.23) * mm});
            skLineSegment(sketch, "E7.18.11.0", {"start": v(29.23, -34.23) * mm, "end": v(26.23, -35.96) * mm});
            skLineSegment(sketch, "E7.0.11.1", {"start": v(27.01, -27.75) * mm, "end": v(27.01, -24.29) * mm});
            skCircle(sketch, "E7.3.11.1", {"center": v(30.01, -26.02) * mm, "radius": 3 * mm, "construction": true});
            skPoint(sketch, "E7.5.11.1", {"position": v(31.51, -28.62) * mm});
            skLineSegment(sketch, "E7.6.11.1", {"start": v(30.01, -29.49) * mm, "end": v(27.01, -27.75) * mm});
            skLineSegment(sketch, "E7.9.11.1", {"start": v(30.01, -22.56) * mm, "end": v(33.01, -24.29) * mm});
            skLineSegment(sketch, "E7.12.11.1", {"start": v(27.01, -24.29) * mm, "end": v(30.01, -22.56) * mm});
            skLineSegment(sketch, "E7.15.11.1", {"start": v(33.01, -24.29) * mm, "end": v(33.01, -27.75) * mm});
            skLineSegment(sketch, "E7.18.11.1", {"start": v(33.01, -27.75) * mm, "end": v(30.01, -29.49) * mm});
            skLineSegment(sketch, "E7.0.11.2", {"start": v(30.8, -21.28) * mm, "end": v(30.8, -17.81) * mm});
            skCircle(sketch, "E7.3.11.2", {"center": v(33.8, -19.55) * mm, "radius": 3 * mm, "construction": true});
            skPoint(sketch, "E7.5.11.2", {"position": v(35.3, -22.14) * mm});
            skLineSegment(sketch, "E7.6.11.2", {"start": v(33.8, -23) * mm, "end": v(30.8, -21.28) * mm});
            skLineSegment(sketch, "E7.9.11.2", {"start": v(33.8, -16.08) * mm, "end": v(36.8, -17.81) * mm});
            skLineSegment(sketch, "E7.12.11.2", {"start": v(30.8, -17.81) * mm, "end": v(33.8, -16.08) * mm});
            skLineSegment(sketch, "E7.15.11.2", {"start": v(36.8, -17.81) * mm, "end": v(36.8, -21.28) * mm});
            skLineSegment(sketch, "E7.18.11.2", {"start": v(36.8, -21.28) * mm, "end": v(33.8, -23) * mm});
            skLineSegment(sketch, "E7.0.11.3", {"start": v(34.58, -14.8) * mm, "end": v(34.58, -11.34) * mm});
            skCircle(sketch, "E7.3.11.3", {"center": v(37.58, -13.07) * mm, "radius": 3 * mm, "construction": true});
            skPoint(sketch, "E7.5.11.3", {"position": v(39.08, -15.67) * mm});
            skLineSegment(sketch, "E7.6.11.3", {"start": v(37.58, -16.53) * mm, "end": v(34.58, -14.8) * mm});
            skLineSegment(sketch, "E7.9.11.3", {"start": v(37.58, -9.6) * mm, "end": v(40.58, -11.34) * mm});
            skLineSegment(sketch, "E7.12.11.3", {"start": v(34.58, -11.34) * mm, "end": v(37.58, -9.6) * mm});
            skLineSegment(sketch, "E7.15.11.3", {"start": v(40.58, -11.34) * mm, "end": v(40.58, -14.8) * mm});
            skLineSegment(sketch, "E7.18.11.3", {"start": v(40.58, -14.8) * mm, "end": v(37.58, -16.53) * mm});
            skLineSegment(sketch, "E7.0.11.4", {"start": v(38.36, -8.33) * mm, "end": v(38.36, -4.86) * mm});
            skCircle(sketch, "E7.3.11.4", {"center": v(41.36, -6.6) * mm, "radius": 3 * mm, "construction": true});
            skPoint(sketch, "E7.5.11.4", {"position": v(42.86, -9.2) * mm});
            skLineSegment(sketch, "E7.6.11.4", {"start": v(41.36, -10.06) * mm, "end": v(38.36, -8.33) * mm});
            skLineSegment(sketch, "E7.9.11.4", {"start": v(41.36, -3.13) * mm, "end": v(44.36, -4.86) * mm});
            skLineSegment(sketch, "E7.12.11.4", {"start": v(38.36, -4.86) * mm, "end": v(41.36, -3.13) * mm});
            skLineSegment(sketch, "E7.15.11.4", {"start": v(44.36, -4.86) * mm, "end": v(44.36, -8.33) * mm});
            skLineSegment(sketch, "E7.18.11.4", {"start": v(44.36, -8.33) * mm, "end": v(41.36, -10.06) * mm});
            skLineSegment(sketch, "E7.0.11.5", {"start": v(42.15, -1.85) * mm, "end": v(42.15, 1.62) * mm});
            skCircle(sketch, "E7.3.11.5", {"center": v(45.15, -0.12) * mm, "radius": 3 * mm, "construction": true});
            skPoint(sketch, "E7.5.11.5", {"position": v(46.65, -2.72) * mm});
            skLineSegment(sketch, "E7.6.11.5", {"start": v(45.15, -3.58) * mm, "end": v(42.15, -1.85) * mm});
            skLineSegment(sketch, "E7.9.11.5", {"start": v(45.15, 3.35) * mm, "end": v(48.15, 1.62) * mm});
            skLineSegment(sketch, "E7.12.11.5", {"start": v(42.15, 1.62) * mm, "end": v(45.15, 3.35) * mm});
            skLineSegment(sketch, "E7.15.11.5", {"start": v(48.15, 1.62) * mm, "end": v(48.15, -1.85) * mm});
            skLineSegment(sketch, "E7.18.11.5", {"start": v(48.15, -1.85) * mm, "end": v(45.15, -3.58) * mm});
            skLineSegment(sketch, "E7.0.11.6", {"start": v(45.93, 4.63) * mm, "end": v(45.93, 8.1) * mm});
            skCircle(sketch, "E7.3.11.6", {"center": v(48.93, 6.36) * mm, "radius": 3 * mm, "construction": true});
            skPoint(sketch, "E7.5.11.6", {"position": v(50.43, 3.76) * mm});
            skLineSegment(sketch, "E7.6.11.6", {"start": v(48.93, 2.9) * mm, "end": v(45.93, 4.63) * mm});
            skLineSegment(sketch, "E7.9.11.6", {"start": v(48.93, 9.82) * mm, "end": v(51.93, 8.1) * mm});
            skLineSegment(sketch, "E7.12.11.6", {"start": v(45.93, 8.1) * mm, "end": v(48.93, 9.82) * mm});
            skLineSegment(sketch, "E7.15.11.6", {"start": v(51.93, 8.1) * mm, "end": v(51.93, 4.63) * mm});
            skLineSegment(sketch, "E7.18.11.6", {"start": v(51.93, 4.63) * mm, "end": v(48.93, 2.9) * mm});
            skLineSegment(sketch, "E7.0.11.7", {"start": v(49.71, 11.1) * mm, "end": v(49.71, 14.57) * mm});
            skCircle(sketch, "E7.3.11.7", {"center": v(52.71, 12.84) * mm, "radius": 3 * mm, "construction": true});
            skPoint(sketch, "E7.5.11.7", {"position": v(54.21, 10.24) * mm});
            skLineSegment(sketch, "E7.6.11.7", {"start": v(52.71, 9.37) * mm, "end": v(49.71, 11.1) * mm});
            skLineSegment(sketch, "E7.9.11.7", {"start": v(52.71, 16.3) * mm, "end": v(55.71, 14.57) * mm});
            skLineSegment(sketch, "E7.12.11.7", {"start": v(49.71, 14.57) * mm, "end": v(52.71, 16.3) * mm});
            skLineSegment(sketch, "E7.15.11.7", {"start": v(55.71, 14.57) * mm, "end": v(55.71, 11.1) * mm});
            skLineSegment(sketch, "E7.18.11.7", {"start": v(55.71, 11.1) * mm, "end": v(52.71, 9.37) * mm});
            skLineSegment(sketch, "E7.0.11.8", {"start": v(53.5, 17.58) * mm, "end": v(53.5, 21.04) * mm});
            skCircle(sketch, "E7.3.11.8", {"center": v(56.5, 19.31) * mm, "radius": 3 * mm, "construction": true});
            skPoint(sketch, "E7.5.11.8", {"position": v(58, 16.71) * mm});
            skLineSegment(sketch, "E7.6.11.8", {"start": v(56.5, 15.85) * mm, "end": v(53.5, 17.58) * mm});
            skLineSegment(sketch, "E7.9.11.8", {"start": v(56.5, 22.78) * mm, "end": v(59.5, 21.04) * mm});
            skLineSegment(sketch, "E7.12.11.8", {"start": v(53.5, 21.04) * mm, "end": v(56.5, 22.78) * mm});
            skLineSegment(sketch, "E7.15.11.8", {"start": v(59.5, 21.04) * mm, "end": v(59.5, 17.58) * mm});
            skLineSegment(sketch, "E7.18.11.8", {"start": v(59.5, 17.58) * mm, "end": v(56.5, 15.85) * mm});
            skLineSegment(sketch, "E7.0.11.9", {"start": v(57.28, 24.06) * mm, "end": v(57.28, 27.52) * mm});
            skCircle(sketch, "E7.3.11.9", {"center": v(60.28, 25.79) * mm, "radius": 3 * mm, "construction": true});
            skPoint(sketch, "E7.5.11.9", {"position": v(61.78, 23.19) * mm});
            skLineSegment(sketch, "E7.6.11.9", {"start": v(60.28, 22.32) * mm, "end": v(57.28, 24.06) * mm});
            skLineSegment(sketch, "E7.9.11.9", {"start": v(60.28, 29.25) * mm, "end": v(63.28, 27.52) * mm});
            skLineSegment(sketch, "E7.12.11.9", {"start": v(57.28, 27.52) * mm, "end": v(60.28, 29.25) * mm});
            skLineSegment(sketch, "E7.15.11.9", {"start": v(63.28, 27.52) * mm, "end": v(63.28, 24.06) * mm});
            skLineSegment(sketch, "E7.18.11.9", {"start": v(63.28, 24.06) * mm, "end": v(60.28, 22.32) * mm});
            skLineSegment(sketch, "E7.0.11.10", {"start": v(61.06, 30.53) * mm, "end": v(61.06, 34) * mm});
            skCircle(sketch, "E7.3.11.10", {"center": v(64.06, 32.26) * mm, "radius": 3 * mm, "construction": true});
            skPoint(sketch, "E7.5.11.10", {"position": v(65.56, 29.67) * mm});
            skLineSegment(sketch, "E7.6.11.10", {"start": v(64.06, 28.8) * mm, "end": v(61.06, 30.53) * mm});
            skLineSegment(sketch, "E7.9.11.10", {"start": v(64.06, 35.73) * mm, "end": v(67.06, 34) * mm});
            skLineSegment(sketch, "E7.12.11.10", {"start": v(61.06, 34) * mm, "end": v(64.06, 35.73) * mm});
            skLineSegment(sketch, "E7.15.11.10", {"start": v(67.06, 34) * mm, "end": v(67.06, 30.53) * mm});
            skLineSegment(sketch, "E7.18.11.10", {"start": v(67.06, 30.53) * mm, "end": v(64.06, 28.8) * mm});
            skLineSegment(sketch, "E7.0.11.11", {"start": v(64.84, 37) * mm, "end": v(64.84, 40.47) * mm});
            skCircle(sketch, "E7.3.11.11", {"center": v(67.84, 38.74) * mm, "radius": 3 * mm, "construction": true});
            skPoint(sketch, "E7.5.11.11", {"position": v(69.34, 36.14) * mm});
            skLineSegment(sketch, "E7.6.11.11", {"start": v(67.84, 35.28) * mm, "end": v(64.84, 37) * mm});
            skLineSegment(sketch, "E7.9.11.11", {"start": v(67.84, 42.2) * mm, "end": v(70.84, 40.47) * mm});
            skLineSegment(sketch, "E7.12.11.11", {"start": v(64.84, 40.47) * mm, "end": v(67.84, 42.2) * mm});
            skLineSegment(sketch, "E7.15.11.11", {"start": v(70.84, 40.47) * mm, "end": v(70.84, 37) * mm});
            skLineSegment(sketch, "E7.18.11.11", {"start": v(70.84, 37) * mm, "end": v(67.84, 35.28) * mm});
            skCircle(sketch, "E8", {"center": v(0, 0) * mm, "radius": 36.79 * mm});
            skSolve(sketch);
        }
        {
            var Q0;
            {var subQ96=sQuery(id+"F5.wireOp",EDGE,"E5.0.5.6");Q0=makeQuery(id+"F5.imprint","IMPRINT",FACE,{"disambiguationData":[TD([[makeQuery(id+"F5.imprint","IMPRINT",EDGE,{"derivedFrom":subQ96}),1.0]])]});}
            extrude(context, id + "F6", {"entities" : qUnion([Q0]), "operationType" : NewBodyOperationType.ADD, "depth" : 2 * mm, "offsetDistance" : 25 * mm});
        }
    });
